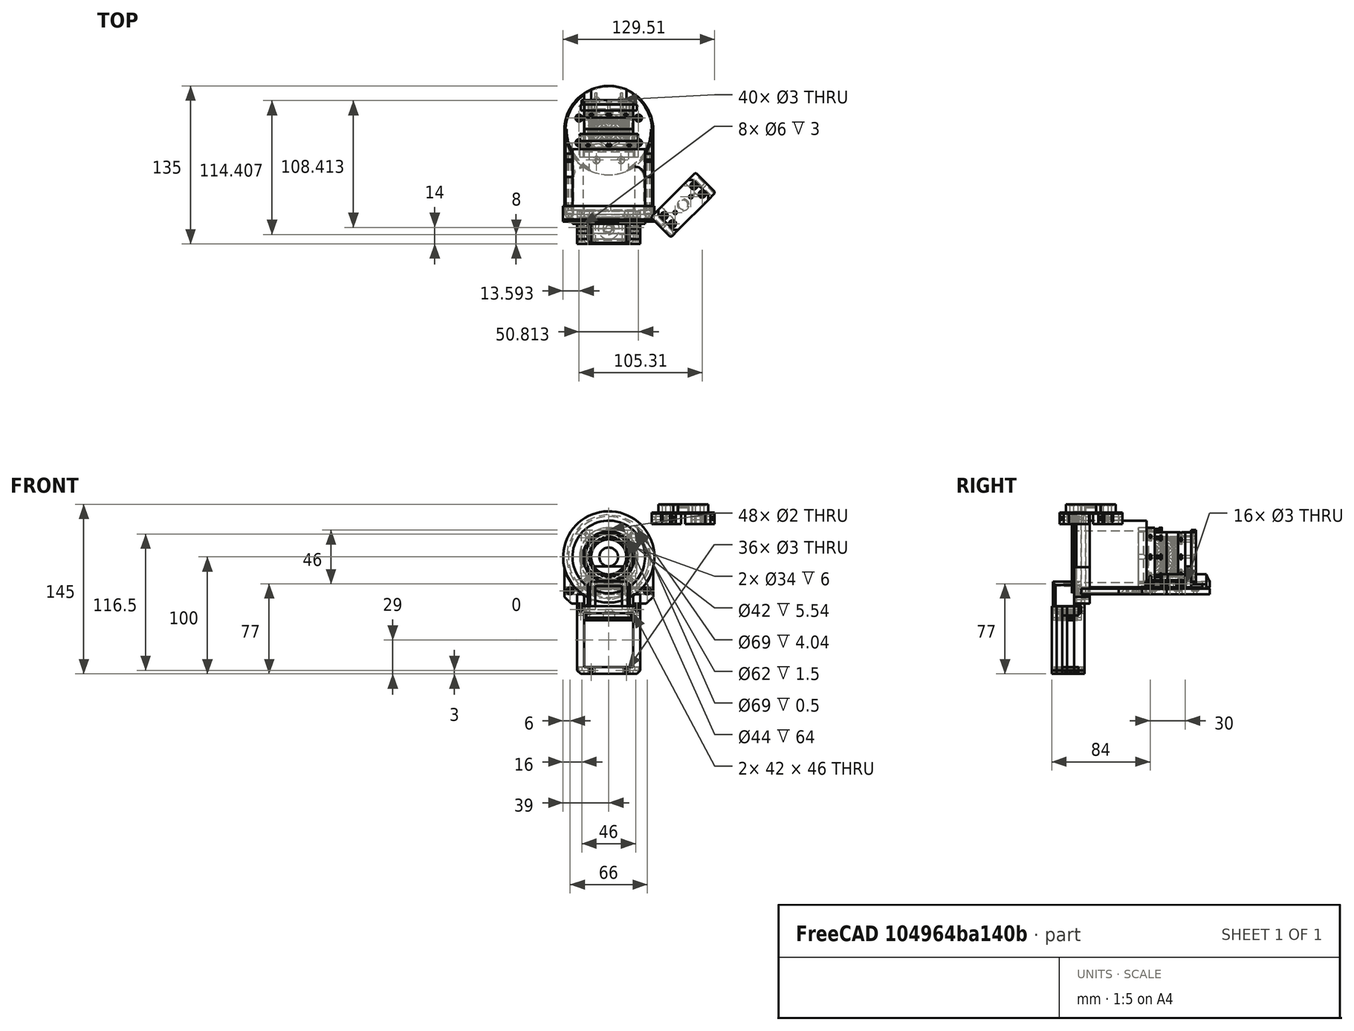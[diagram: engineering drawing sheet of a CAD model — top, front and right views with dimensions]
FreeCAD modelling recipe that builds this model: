
FCSTD DOCUMENT  (FreeCAD 0.19R24276 (Git))
Label: G-mini_encoder-holder_026
License: All rights reserved
LicenseURL: http://en.wikipedia.org/wiki/All_rights_reserved
objects: Part::Cylinder×239, Part::Cut×117, Part::Compound×116, Part::Box×114, Part::Chamfer×42, Part::FeaturePython×24, Mesh::Feature×17, Part::Common×9, Part::Torus×2
note: 663 computed .brp shape members not serialized (recipe doc carries the construction recipe); baked Part::Feature solids carry a one-line shape summary decoded from their .brp

FEATURE [Part::Box] Box883  label="Krychle882"
  AttacherType = Attacher::AttachEngine3D
  Height = 32
  Length = 15
  Placement = pos=(-38,-68,5) rot=(0,0,1;0rad)
  Width = 13.5
FEATURE [Part::Box] Box908  label="Krychle907"
  AttacherType = Attacher::AttachEngine3D
  Height = 6
  Length = 8
  Placement = pos=(-38,-79,5) rot=(0,0,1;0rad)
  Width = 80
FEATURE [Part::Box] Box909  label="Krychle908"
  AttacherType = Attacher::AttachEngine3D
  Height = 6
  Length = 8
  Placement = pos=(30,-79,5) rot=(0,0,1;0rad)
  Width = 80
FEATURE [Part::Box] Box910  label="Krychle909"
  AttacherType = Attacher::AttachEngine3D
  Height = 6
  Length = 20
  Placement = pos=(-38,-40,5) rot=(0,0,1;0rad)
  Width = 20
FEATURE [Part::Cylinder] Cylinder2670  label="Válec2640"
  Angle = 360
  AttacherType = Attacher::AttachEngine3D
  Height = 16
  Placement = pos=(-22,-40,0) rot=(0,0,1;0rad)
  Radius = 8
FEATURE [Part::Cylinder] Cylinder2671  label="Válec2641"
  Angle = 360
  AttacherType = Attacher::AttachEngine3D
  Height = 16
  Placement = pos=(22,-40,0) rot=(0,0,1;0rad)
  Radius = 8
FEATURE [Part::Box] Box911  label="Krychle910"
  AttacherType = Attacher::AttachEngine3D
  Height = 6
  Length = 20
  Placement = pos=(18,-40,5) rot=(0,0,1;0rad)
  Width = 20
FEATURE [Part::Cylinder] Cylinder2672  label="Válec2642"
  Angle = 360
  AttacherType = Attacher::AttachEngine3D
  Height = 16
  Radius = 36
FEATURE [Part::Cylinder] Cylinder2673  label="Válec2643"
  Angle = 360
  AttacherType = Attacher::AttachEngine3D
  Height = 16
  Radius = 36
FEATURE [Part::Cylinder] Cylinder2674  label="Válec2644"
  Angle = 360
  AttacherType = Attacher::AttachEngine3D
  Height = 16
  Radius = 36
FEATURE [Part::Chamfer] Chamfer132
  Base = -> Box908
  Edges = 1 edges r=1: [Edge2]
FEATURE [Part::Chamfer] Chamfer133
  Base = -> Box909
  Edges = 1 edges r=1: [Edge6]
FEATURE [Part::Compound] Compound1181
  Links = -> [Box911,Box910]
FEATURE [Part::Compound] Compound1182
  Links = -> [Cylinder2671,Cylinder2670]
FEATURE [Part::Chamfer] Chamfer135
  Base = -> Chamfer133
  Edges = 1 edges r=1: [Edge15]
FEATURE [Part::Chamfer] Chamfer139
  Base = -> Chamfer132
  Edges = 1 edges r=1: [Edge15]
FEATURE [Part::Cut] Cut996
  Base = -> Chamfer135
  Tool = -> Cylinder2674
FEATURE [Part::Cut] Cut994
  Base = -> Chamfer139
  Tool = -> Cylinder2672
FEATURE [Part::Cut] Cut993
  Base = -> Compound1181
  Tool = -> Compound1182
FEATURE [Part::Chamfer] Chamfer134
  Base = -> Cut993
  Edges = 1 edges r=1: [Edge8]
FEATURE [Part::Chamfer] Chamfer136
  Base = -> Chamfer134
  Edges = 1 edges r=1: [Edge8]
FEATURE [Part::Chamfer] Chamfer137
  Base = -> Chamfer136
  Edges = 1 edges r=1: [Edge23]
FEATURE [Part::Chamfer] Chamfer138
  Base = -> Chamfer137
  Edges = 1 edges r=1: [Edge16]
FEATURE [Part::Cut] Cut995
  Base = -> Chamfer138
  Tool = -> Cylinder2673
FEATURE [Part::Box] Box884  label="Krychle883"
  AttacherType = Attacher::AttachEngine3D
  Height = 32
  Length = 15
  Placement = pos=(23,-68,5) rot=(0,0,1;0rad)
  Width = 13.5
FEATURE [Part::Cylinder] Cylinder2630  label="Válec2600"
  Angle = 360
  AttacherType = Attacher::AttachEngine3D
  Height = 3
  Placement = pos=(-19.4454,-19.4454,19) rot=(0,0,1;2.35619rad)
  Radius = 3
FEATURE [Part::Cylinder] Cylinder2631  label="Válec2601"
  Angle = 360
  AttacherType = Attacher::AttachEngine3D
  Height = 5
  Placement = pos=(1.1e-14,-27.5,19.5) rot=(0,0,1;3.14159rad)
  Radius = 3
FEATURE [Part::Cylinder] Cylinder2632  label="Válec2602"
  Angle = 360
  AttacherType = Attacher::AttachEngine3D
  Height = 20
  Placement = pos=(-19.4454,19.4454,19) rot=(0,0,1;0.785398rad)
  Radius = 1.5
FEATURE [Part::Cylinder] Cylinder2633  label="Válec2603"
  Angle = 360
  AttacherType = Attacher::AttachEngine3D
  Height = 20
  Placement = pos=(-19.4454,-19.4454,19) rot=(0,0,1;2.35619rad)
  Radius = 1.5
FEATURE [Part::Cylinder] Cylinder2634  label="Válec2604"
  Angle = 360
  AttacherType = Attacher::AttachEngine3D
  Height = 20
  Placement = pos=(19.4454,-19.4454,19) rot=(0,0,1;3.92699rad)
  Radius = 1.5
FEATURE [Part::Cylinder] Cylinder2635  label="Válec2605"
  Angle = 360
  AttacherType = Attacher::AttachEngine3D
  Height = 3
  Placement = pos=(-19.45,19.45,19) rot=(0,0,1;0.785398rad)
  Radius = 3
FEATURE [Part::Cylinder] Cylinder2636  label="Válec2606"
  Angle = 360
  AttacherType = Attacher::AttachEngine3D
  Height = 3
  Placement = pos=(-27.5,-4e-15,19) rot=(0,0,1;1.5708rad)
  Radius = 3
FEATURE [Part::Cylinder] Cylinder2637  label="Válec2607"
  Angle = 360
  AttacherType = Attacher::AttachEngine3D
  Height = 5
  Placement = pos=(19.45,-19.45,19.5) rot=(0,0,1;3.92699rad)
  Radius = 3
FEATURE [Part::Cylinder] Cylinder2638  label="Válec2608"
  Angle = 360
  AttacherType = Attacher::AttachEngine3D
  Height = 3
  Placement = pos=(27.5,1.2e-14,19) rot=(0,0,-1;1.5708rad)
  Radius = 3
FEATURE [Part::Cylinder] Cylinder2639  label="Válec2609"
  Angle = 360
  AttacherType = Attacher::AttachEngine3D
  Height = 3
  Placement = pos=(19.4454,19.4454,19) rot=(0,0,-1;0.785398rad)
  Radius = 3
FEATURE [Part::FeaturePython] Tube120  # WARN: FeaturePython — macro-defined, semantics opaque (R4)
  AttacherType = Attacher::AttachEngine3D
  Height = 24
  InnerRadius = 22
  OuterRadius = 31
  Placement = pos=(0,-17,37) rot=(1,0,0;1.5708rad)
FEATURE [Part::Cylinder] Cylinder2640  label="Válec2610"
  Angle = 360
  AttacherType = Attacher::AttachEngine3D
  Height = 20
  Placement = pos=(-27.5,-4e-15,19) rot=(0,0,1;1.5708rad)
  Radius = 1.5
FEATURE [Part::Cylinder] Cylinder2641  label="Válec2611"
  Angle = 360
  AttacherType = Attacher::AttachEngine3D
  Height = 20
  Placement = pos=(1.1e-14,-27.5,19) rot=(0,0,1;3.14159rad)
  Radius = 1.5
FEATURE [Part::Cylinder] Cylinder2642  label="Válec2612"
  Angle = 360
  AttacherType = Attacher::AttachEngine3D
  Height = 3
  Placement = pos=(0,27.5,19) rot=(0,0,1;0rad)
  Radius = 3
FEATURE [Part::Compound] Compound1170
  Links = -> [Cylinder2642,Cylinder2635,Cylinder2636,Cylinder2630,Cylinder2631,Cylinder2637,Cylinder2638,Cylinder2639]
  Placement = pos=(0,0,-19) rot=(0,0,1;0rad)
FEATURE [Part::Cylinder] Cylinder2643  label="Válec2613"
  Angle = 360
  AttacherType = Attacher::AttachEngine3D
  Height = 20
  Placement = pos=(19.4454,19.4454,19) rot=(0,0,-1;0.785398rad)
  Radius = 1.5
FEATURE [Part::Cylinder] Cylinder2644  label="Válec2614"
  Angle = 360
  AttacherType = Attacher::AttachEngine3D
  Height = 20
  Placement = pos=(27.5,1.2e-14,19) rot=(0,0,-1;1.5708rad)
  Radius = 1.5
FEATURE [Part::Cylinder] Cylinder2645  label="Válec2615"
  Angle = 360
  AttacherType = Attacher::AttachEngine3D
  Height = 6
  Radius = 38
FEATURE [Part::Cut] Cut630
  Base = -> Cylinder2645
  Tool = -> Compound1170
FEATURE [Part::Cylinder] Cylinder2646  label="Válec2616"
  Angle = 360
  AttacherType = Attacher::AttachEngine3D
  Height = 20
  Placement = pos=(0,27.5,19) rot=(0,0,1;0rad)
  Radius = 1.5
FEATURE [Part::Compound] Compound1169
  Links = -> [Cylinder2646,Cylinder2632,Cylinder2640,Cylinder2633,Cylinder2641,Cylinder2634,Cylinder2644,Cylinder2643]
  Placement = pos=(0,0,-23) rot=(0,0,1;0rad)
FEATURE [Part::Cut] Cut628
  Base = -> Cut630
  Tool = -> Compound1169
FEATURE [Part::Cylinder] Cylinder2647  label="Válec2617"
  Angle = 360
  AttacherType = Attacher::AttachEngine3D
  Height = 5
  Placement = pos=(0,0,1) rot=(0,0,1;0rad)
  Radius = 14
FEATURE [Part::Cut] Cut629
  Base = -> Cut628
  Tool = -> Cylinder2647
FEATURE [Part::Chamfer] Chamfer126
  Base = -> Cut629
  Edges = 1 edges r=1: [Edge3]
  Placement = pos=(1e-15,0,11) rot=(-0.19509,0.980785,0;3.14159rad)
FEATURE [Part::Cut] Cut976
  Base = -> Chamfer126
  Tool = -> Tube120
FEATURE [Part::Compound] Compound
  Links = -> [Box884,Box883]
  Placement = pos=(0,-17.5,0) rot=(0,0,1;0rad)
FEATURE [Part::Box] Box912  label="Krychle911"
  AttacherType = Attacher::AttachEngine3D
  Height = 40
  Length = 17
  Placement = pos=(21,-68,-3) rot=(0,0,1;0rad)
  Width = 13.5
FEATURE [Part::Box] Box913  label="Krychle912"
  AttacherType = Attacher::AttachEngine3D
  Height = 40
  Length = 17
  Placement = pos=(-38,-68,-3) rot=(0,0,1;0rad)
  Width = 13.5
FEATURE [Part::Compound] Compound1184
  Links = -> [Box912,Box913]
  Placement = pos=(0,-6,0) rot=(0,0,1;0rad)
FEATURE [Part::Compound] Compound1185
  Links = -> [Cut996,Cut994]
FEATURE [Part::Cylinder] Cylinder2621  label="Válec2591"
  Angle = 360
  AttacherType = Attacher::AttachEngine3D
  Height = 50
  Placement = pos=(-34,-10,8) rot=(1,0,0;1.5708rad)
  Radius = 1.5
FEATURE [Part::Cylinder] Cylinder2622  label="Válec2592"
  Angle = 360
  AttacherType = Attacher::AttachEngine3D
  Height = 8
  Placement = pos=(-34,-61,8) rot=(1,0,0;1.5708rad)
  Radius = 3
FEATURE [Part::Cylinder] Cylinder2623  label="Válec2593"
  Angle = 360
  AttacherType = Attacher::AttachEngine3D
  Height = 50
  Placement = pos=(34,-10,8) rot=(1,0,0;1.5708rad)
  Radius = 1.5
FEATURE [Part::Cylinder] Cylinder2624  label="Válec2594"
  Angle = 360
  AttacherType = Attacher::AttachEngine3D
  Height = 8
  Placement = pos=(34,-61,8) rot=(1,0,0;1.5708rad)
  Radius = 3
FEATURE [Part::Compound] Compound1186
  Links = -> [Cylinder2621,Cylinder2623]
  Placement = pos=(0,-11,0) rot=(0,0,1;0rad)
FEATURE [Part::Compound] Compound1187
  Links = -> [Cylinder2622,Cylinder2624]
  Placement = pos=(0,-5,0) rot=(0,0,1;0rad)
FEATURE [Part::Cylinder] Cylinder2675  label="Válec2645"
  Angle = 360
  AttacherType = Attacher::AttachEngine3D
  Height = 16
  Radius = 38
FEATURE [Part::Cylinder] Cylinder2676  label="Válec2646"
  Angle = 360
  AttacherType = Attacher::AttachEngine3D
  Height = 16
  Radius = 38
FEATURE [Part::Box] Box914  label="Krychle913"
  AttacherType = Attacher::AttachEngine3D
  Height = 6
  Length = 8
  Placement = pos=(-38,-68,5) rot=(0,0,1;0rad)
  Width = 69
FEATURE [Part::Box] Box915  label="Krychle914"
  AttacherType = Attacher::AttachEngine3D
  Height = 6
  Length = 8
  Placement = pos=(30,-68,5) rot=(0,0,1;0rad)
  Width = 69
FEATURE [Part::Chamfer] Chamfer142
  Base = -> Box915
  Edges = 1 edges r=1: [Edge6]
FEATURE [Part::Chamfer] Chamfer140
  Base = -> Chamfer142
  Edges = 1 edges r=1: [Edge15]
FEATURE [Part::Chamfer] Chamfer143
  Base = -> Box914
  Edges = 1 edges r=1: [Edge2]
FEATURE [Part::Chamfer] Chamfer141
  Base = -> Chamfer143
  Edges = 1 edges r=1: [Edge15]
FEATURE [Part::Cut] Cut997
  Base = -> Chamfer141
  Tool = -> Cylinder2675
FEATURE [Part::Cut] Cut998
  Base = -> Chamfer140
  Tool = -> Cylinder2676
FEATURE [Part::Compound] Compound1188
  Links = -> [Cut998,Cut997]
FEATURE [Part::Cut] Cut
  Base = -> Compound1184
  Tool = -> Compound1188
FEATURE [Part::Cylinder] Cylinder2650  label="Válec2620"
  Angle = 360
  AttacherType = Attacher::AttachEngine3D
  Height = 60
  Placement = pos=(24,73,-80) rot=(0,0,1;0rad)
  Radius = 1.5
FEATURE [Part::Cylinder] Cylinder2651  label="Válec2621"
  Angle = 360
  AttacherType = Attacher::AttachEngine3D
  Height = 60
  Placement = pos=(-24,73,-80) rot=(0,0,1;0rad)
  Radius = 1.5
FEATURE [Part::Cylinder] Cylinder2652  label="Válec2622"
  Angle = 360
  AttacherType = Attacher::AttachEngine3D
  Height = 60
  Placement = pos=(-15,125,-80) rot=(0,0,1;0rad)
  Radius = 1.5
FEATURE [Part::Cylinder] Cylinder2653  label="Válec2623"
  Angle = 360
  AttacherType = Attacher::AttachEngine3D
  Height = 60
  Placement = pos=(15,125,-80) rot=(0,0,1;0rad)
  Radius = 1.5
FEATURE [Part::Box] Box893  label="Krychle892"
  AttacherType = Attacher::AttachEngine3D
  Height = 9
  Length = 54
  Placement = pos=(-27,60,76) rot=(0,0,1;0rad)
  Width = 68
FEATURE [Part::Box] Box894  label="Krychle893"
  AttacherType = Attacher::AttachEngine3D
  Height = 50
  Length = 42
  Placement = pos=(-21,58,40) rot=(0,0,1;0rad)
  Width = 64
FEATURE [Part::Cut] Cut978
  Base = -> Box893
  Placement = pos=(0,0,-9) rot=(0,0,1;0rad)
  Tool = -> Box894
FEATURE [Part::Compound] Compound1172
  Links = -> [Cylinder2650,Cylinder2651,Cylinder2652,Cylinder2653]
  Placement = pos=(0,0,120) rot=(0,0,1;0rad)
FEATURE [Part::Chamfer] Chamfer127
  Base = -> Cut978
  Edges = 2 edges r=3: [Edge3,Edge15]
FEATURE [Part::Cut] Cut979
  Base = -> Chamfer127
  Tool = -> Compound1172
FEATURE [Part::Box] Box904  label="Krychle903"
  AttacherType = Attacher::AttachEngine3D
  Height = 2
  Length = 7
  Placement = pos=(-28,70,-48) rot=(0,0,1;0rad)
  Width = 6
FEATURE [Part::Box] Box905  label="Krychle904"
  AttacherType = Attacher::AttachEngine3D
  Height = 2
  Length = 6
  Placement = pos=(-18,122,-48) rot=(0,0,1;0rad)
  Width = 6
FEATURE [Part::Box] Box906  label="Krychle905"
  AttacherType = Attacher::AttachEngine3D
  Height = 2
  Length = 6
  Placement = pos=(21,70,-48) rot=(0,0,1;0rad)
  Width = 6
FEATURE [Part::Box] Box907  label="Krychle906"
  AttacherType = Attacher::AttachEngine3D
  Height = 2
  Length = 6
  Placement = pos=(12,122,-48) rot=(0,0,1;0rad)
  Width = 6
FEATURE [Part::Compound] Compound1179
  Links = -> [Box904,Box905,Box906,Box907]
  Placement = pos=(0,0,118) rot=(0,0,1;0rad)
FEATURE [Part::Cut] Cut989
  Base = -> Cut979
  Placement = pos=(0,2,65) rot=(0,0.707107,-0.707107;3.14159rad)
  Tool = -> Compound1179
FEATURE [Part::Torus] Torus004  label="Anuloid004"
  Angle1 = -180
  Angle2 = 180
  Angle3 = 360
  AttacherType = Attacher::AttachEngine3D
  Placement = pos=(17,-98,10) rot=(1,0,0;1.5708rad)
  Radius1 = 34.1
  Radius2 = 2
FEATURE [Part::FeaturePython] Tube115  # WARN: FeaturePython — macro-defined, semantics opaque (R4)
  AttacherType = Attacher::AttachEngine3D
  Height = 11.5
  InnerRadius = 34.5
  OuterRadius = 39
  Placement = pos=(17,-92,10) rot=(1,0,0;1.5708rad)
FEATURE [Part::FeaturePython] Tube116  # WARN: FeaturePython — macro-defined, semantics opaque (R4)
  AttacherType = Attacher::AttachEngine3D
  Height = 0.5
  InnerRadius = 34.5
  OuterRadius = 39
  Placement = pos=(17,-93.5,10) rot=(1,0,0;1.5708rad)
FEATURE [Part::FeaturePython] Tube117  # WARN: FeaturePython — macro-defined, semantics opaque (R4)
  AttacherType = Attacher::AttachEngine3D
  Height = 1.5
  InnerRadius = 31
  OuterRadius = 39
  Placement = pos=(17,-92,10) rot=(1,0,0;1.5708rad)
FEATURE [Part::Cut] Cut969
  Base = -> Tube115
  Tool = -> Torus004
FEATURE [Part::Compound] Compound1161
  Links = -> [Tube117,Tube116]
FEATURE [Part::Cylinder] Cylinder2620  label="Válec2590"
  Angle = 360
  AttacherType = Attacher::AttachEngine3D
  Height = 10
  Placement = pos=(17,-98,44) rot=(1,0,0;1.5708rad)
  Radius = 2
FEATURE [Part::Cut] Cut970
  Base = -> Cut969
  Placement = pos=(0,-2,0) rot=(0,0,1;0rad)
  Tool = -> Cylinder2620
FEATURE [Part::Compound] Compound1162  label="Wrist_outer-halo-ring"
  Links = -> [Cut970,Compound1161]
  Placement = pos=(-17,-166,47) rot=(1,0,0;3.14159rad)
FEATURE [Part::Cylinder] Cylinder  label="Válec"
  Angle = 360
  AttacherType = Attacher::AttachEngine3D
  Height = 20
  Placement = pos=(0,-54,37) rot=(1,0,0;1.5708rad)
  Radius = 39
FEATURE [Part::Cut] Cut999
  Base = -> Cut
  Tool = -> Cylinder
FEATURE [Part::Chamfer] Chamfer
  Base = -> Cut999
  Edges = 2 edges r=6: [Edge18,Edge36]
FEATURE [Part::FeaturePython] Tube121  # WARN: FeaturePython — macro-defined, semantics opaque (R4)
  AttacherType = Attacher::AttachEngine3D
  Height = 64
  InnerRadius = 22
  OuterRadius = 31
  Placement = pos=(0,-16,37) rot=(1,0,0;1.5708rad)
FEATURE [Part::Cylinder] Cylinder2677  label="Válec2647"
  Angle = 360
  AttacherType = Attacher::AttachEngine3D
  Height = 3
  Placement = pos=(-33,-61,8) rot=(1,0,0;1.5708rad)
  Radius = 3
FEATURE [Part::Cylinder] Cylinder2678  label="Válec2648"
  Angle = 360
  AttacherType = Attacher::AttachEngine3D
  Height = 3
  Placement = pos=(33,-61,8) rot=(1,0,0;1.5708rad)
  Radius = 3
FEATURE [Part::Compound] Compound1189
  Links = -> [Cylinder2677,Cylinder2678]
  Placement = pos=(0,-10,0) rot=(0,0,1;0rad)
FEATURE [Part::Cylinder] Cylinder2679  label="Válec2649"
  Angle = 360
  AttacherType = Attacher::AttachEngine3D
  Height = 60
  Placement = pos=(-33,-10,8) rot=(1,0,0;1.5708rad)
  Radius = 1.5
FEATURE [Part::Cylinder] Cylinder2680  label="Válec2650"
  Angle = 360
  AttacherType = Attacher::AttachEngine3D
  Height = 60
  Placement = pos=(33,-10,8) rot=(1,0,0;1.5708rad)
  Radius = 1.5
FEATURE [Part::Compound] Compound1190
  Links = -> [Cylinder2679,Cylinder2680]
  Placement = pos=(0,-4,0) rot=(0,0,1;0rad)
FEATURE [Part::Cut] Cut1000
  Base = -> Chamfer
  Tool = -> Compound1189
FEATURE [Part::Cut] Cut1001
  Base = -> Cut1000
  Tool = -> Compound1190
FEATURE [Part::Cut] Cut1002
  Base = -> Compound1185
  Tool = -> Compound
FEATURE [Part::Box] Box  label="Krychle"
  AttacherType = Attacher::AttachEngine3D
  Height = 6
  Length = 6
  Placement = pos=(30,-27,5) rot=(0,0,1;0rad)
  Width = 2
FEATURE [Part::Box] Box916  label="Krychle915"
  AttacherType = Attacher::AttachEngine3D
  Height = 6
  Length = 6
  Placement = pos=(-36,-27,5) rot=(0,0,1;0rad)
  Width = 2
FEATURE [Part::Compound] Compound1191
  Links = -> [Box,Box916]
FEATURE [Part::Cut] Cut1003
  Base = -> Cut1002
  Tool = -> Compound1191
FEATURE [Part::Box] Box917  label="Krychle916"
  AttacherType = Attacher::AttachEngine3D
  Height = 6
  Length = 6
  Placement = pos=(30,-27,5) rot=(0,0,1;0rad)
  Width = 2
FEATURE [Part::Box] Box918  label="Krychle917"
  AttacherType = Attacher::AttachEngine3D
  Height = 6
  Length = 6
  Placement = pos=(-36,-27,5) rot=(0,0,1;0rad)
  Width = 2
FEATURE [Part::Compound] Compound1192
  Links = -> [Box917,Box918]
FEATURE [Part::Cut] Cut1004
  Base = -> Cut995
  Tool = -> Compound1192
FEATURE [Part::Cylinder] Cylinder2681  label="Válec2651"
  Angle = 360
  AttacherType = Attacher::AttachEngine3D
  Height = 60
  Placement = pos=(-33,-10,8) rot=(1,0,0;1.5708rad)
  Radius = 1.5
FEATURE [Part::Cylinder] Cylinder2682  label="Válec2652"
  Angle = 360
  AttacherType = Attacher::AttachEngine3D
  Height = 60
  Placement = pos=(33,-10,8) rot=(1,0,0;1.5708rad)
  Radius = 1.5
FEATURE [Part::Compound] Compound1193
  Links = -> [Cylinder2681,Cylinder2682]
  Placement = pos=(0,-1,0) rot=(0,0,1;0rad)
FEATURE [Part::Cylinder] Cylinder2683  label="Válec2653"
  Angle = 360
  AttacherType = Attacher::AttachEngine3D
  Height = 100
  Placement = pos=(-33,-10,8) rot=(1,0,0;1.5708rad)
  Radius = 1.5
FEATURE [Part::Cylinder] Cylinder2684  label="Válec2654"
  Angle = 360
  AttacherType = Attacher::AttachEngine3D
  Height = 100
  Placement = pos=(33,-10,8) rot=(1,0,0;1.5708rad)
  Radius = 1.5
FEATURE [Part::Compound] Compound1194
  Links = -> [Cylinder2683,Cylinder2684]
  Placement = pos=(0,-1,0) rot=(0,0,1;0rad)
FEATURE [Part::Cut] Cut1005
  Base = -> Cut1003
  Tool = -> Compound1194
FEATURE [Part::Cut] Cut1006
  Base = -> Cut976
  Tool = -> Compound1193
FEATURE [Part::Cylinder] Cylinder2685  label="Válec2655"
  Angle = 360
  AttacherType = Attacher::AttachEngine3D
  Height = 60
  Placement = pos=(-33,-10,8) rot=(1,0,0;1.5708rad)
  Radius = 1.5
FEATURE [Part::Cylinder] Cylinder2686  label="Válec2656"
  Angle = 360
  AttacherType = Attacher::AttachEngine3D
  Height = 60
  Placement = pos=(33,-10,8) rot=(1,0,0;1.5708rad)
  Radius = 1.5
FEATURE [Part::Compound] Compound1195
  Links = -> [Cylinder2685,Cylinder2686]
  Placement = pos=(0,-4,0) rot=(0,0,1;0rad)
FEATURE [Part::Cut] Cut1007
  Base = -> Cut1004
  Tool = -> Compound1195
FEATURE [Part::Box] Box895  label="Krychle894"
  AttacherType = Attacher::AttachEngine3D
  Height = 9
  Length = 54
  Placement = pos=(-27,70,75) rot=(0,0,1;0rad)
  Width = 58
FEATURE [Part::Box] Box896  label="Krychle895"
  AttacherType = Attacher::AttachEngine3D
  Height = 50
  Length = 42
  Placement = pos=(-21,76,38) rot=(0,0,1;0rad)
  Width = 46
FEATURE [Part::Cylinder] Cylinder2658  label="Válec2628"
  Angle = 360
  AttacherType = Attacher::AttachEngine3D
  Height = 60
  Placement = pos=(24,73,-80) rot=(0,0,1;0rad)
  Radius = 1.5
FEATURE [Part::Cylinder] Cylinder2659  label="Válec2629"
  Angle = 360
  AttacherType = Attacher::AttachEngine3D
  Height = 60
  Placement = pos=(-24,73,-80) rot=(0,0,1;0rad)
  Radius = 1.5
FEATURE [Part::Cylinder] Cylinder2660  label="Válec2630"
  Angle = 360
  AttacherType = Attacher::AttachEngine3D
  Height = 60
  Placement = pos=(-15,125,-80) rot=(0,0,1;0rad)
  Radius = 1.5
FEATURE [Part::Cylinder] Cylinder2661  label="Válec2631"
  Angle = 360
  AttacherType = Attacher::AttachEngine3D
  Height = 60
  Placement = pos=(15,125,-80) rot=(0,0,1;0rad)
  Radius = 1.5
FEATURE [Part::Box] Box897  label="Krychle896"
  AttacherType = Attacher::AttachEngine3D
  Height = 10
  Length = 54
  Placement = pos=(-27,70,75) rot=(0,0,1;0rad)
  Width = 58
FEATURE [Part::Box] Box898  label="Krychle897"
  AttacherType = Attacher::AttachEngine3D
  Height = 50
  Length = 42
  Placement = pos=(-21,76,38) rot=(0,0,1;0rad)
  Width = 46
FEATURE [Part::Cylinder] Cylinder2662  label="Válec2632"
  Angle = 360
  AttacherType = Attacher::AttachEngine3D
  Height = 3
  Placement = pos=(-24,128,72) rot=(1,0,0;1.5708rad)
  Radius = 3
FEATURE [Part::Cylinder] Cylinder2663  label="Válec2633"
  Angle = 360
  AttacherType = Attacher::AttachEngine3D
  Height = 3
  Placement = pos=(24,128,72) rot=(1,0,0;1.5708rad)
  Radius = 3
FEATURE [Part::Compound] Compound1174
  Links = -> [Cylinder2658,Cylinder2659,Cylinder2660,Cylinder2661]
  Placement = pos=(0,0,120) rot=(0,0,1;0rad)
FEATURE [Part::Cut] Cut981
  Base = -> Box895
  Placement = pos=(0,0,10) rot=(0,0,1;0rad)
  Tool = -> Box896
FEATURE [Part::Cut] Cut983
  Base = -> Box897
  Tool = -> Box898
FEATURE [Part::Compound] Compound1175
  Links = -> [Cylinder2662,Cylinder2663]
  Placement = pos=(0,0,8) rot=(0,0,1;0rad)
FEATURE [Part::Cylinder] Cylinder2664  label="Válec2634"
  Angle = 360
  AttacherType = Attacher::AttachEngine3D
  Height = 50
  Placement = pos=(-24,140,72) rot=(1,0,0;1.5708rad)
  Radius = 1.5
FEATURE [Part::Cylinder] Cylinder2665  label="Válec2635"
  Angle = 360
  AttacherType = Attacher::AttachEngine3D
  Height = 50
  Placement = pos=(24,140,72) rot=(1,0,0;1.5708rad)
  Radius = 1.5
FEATURE [Part::Compound] Compound1177
  Links = -> [Cylinder2664,Cylinder2665]
  Placement = pos=(0,0,8) rot=(0,0,1;0rad)
FEATURE [Part::Box] Box903  label="Krychle902"
  AttacherType = Attacher::AttachEngine3D
  Height = 10
  Length = 56
  Placement = pos=(-28,78,75) rot=(0,0,1;0rad)
  Width = 44
FEATURE [Part::Cut] Cut984
  Base = -> Cut983
  Tool = -> Box903
FEATURE [Part::Cylinder] Cylinder2666  label="Válec2636"
  Angle = 360
  AttacherType = Attacher::AttachEngine3D
  Height = 60
  Placement = pos=(15,125,-80) rot=(0,0,1;0rad)
  Radius = 1.5
FEATURE [Part::Cylinder] Cylinder2667  label="Válec2637"
  Angle = 360
  AttacherType = Attacher::AttachEngine3D
  Height = 60
  Placement = pos=(24,73,-80) rot=(0,0,1;0rad)
  Radius = 1.5
FEATURE [Part::Cylinder] Cylinder2668  label="Válec2638"
  Angle = 360
  AttacherType = Attacher::AttachEngine3D
  Height = 60
  Placement = pos=(-24,73,-80) rot=(0,0,1;0rad)
  Radius = 1.5
FEATURE [Part::Cylinder] Cylinder2669  label="Válec2639"
  Angle = 360
  AttacherType = Attacher::AttachEngine3D
  Height = 60
  Placement = pos=(-15,125,-80) rot=(0,0,1;0rad)
  Radius = 1.5
FEATURE [Part::Compound] Compound1178
  Links = -> [Cylinder2667,Cylinder2668,Cylinder2669,Cylinder2666]
  Placement = pos=(0,0,120) rot=(0,0,1;0rad)
FEATURE [Part::Cut] Cut985
  Base = -> Cut984
  Tool = -> Compound1178
FEATURE [Part::Chamfer] Chamfer130
  Base = -> Cut981
  Edges = 2 edges r=3: [Edge3,Edge15]
FEATURE [Part::Cut] Cut990
  Base = -> Chamfer130
  Tool = -> Compound1174
FEATURE [Part::Chamfer] Chamfer131
  Base = -> Cut985
  Edges = 2 edges r=3: [Edge32,Edge43]
FEATURE [Part::Cut] Cut991
  Base = -> Chamfer131
  Tool = -> Compound1175
FEATURE [Part::Cut] Cut992
  Base = -> Cut991
  Tool = -> Compound1177
FEATURE [Part::Compound] Compound1180  label="G-mini_encoder-holder-front"
  Links = -> [Cut990,Cut992]
  Placement = pos=(0,1,65) rot=(0,0.707107,-0.707107;3.14159rad)
FEATURE [Part::Box] Box919  label="Krychle918"
  AttacherType = Attacher::AttachEngine3D
  Height = 16
  Length = 12
  Placement = pos=(9,-74,-11) rot=(0,0,1;0rad)
  Width = 9
FEATURE [Part::Box] Box920  label="Krychle919"
  AttacherType = Attacher::AttachEngine3D
  Height = 16
  Length = 12
  Placement = pos=(-21,-74,-11) rot=(0,0,1;0rad)
  Width = 9
FEATURE [Part::Compound] Compound1196
  Links = -> [Box919,Box920]
FEATURE [Part::Cylinder] Cylinder2687  label="Válec2657"
  Angle = 360
  AttacherType = Attacher::AttachEngine3D
  Height = 14
  Placement = pos=(9,-60,-11) rot=(1,0,0;1.5708rad)
  Radius = 12
FEATURE [Part::Cylinder] Cylinder2688  label="Válec2658"
  Angle = 360
  AttacherType = Attacher::AttachEngine3D
  Height = 14
  Placement = pos=(-9,-60,-11) rot=(1,0,0;1.5708rad)
  Radius = 12
FEATURE [Part::Compound] Compound1197
  Links = -> [Cylinder2687,Cylinder2688]
FEATURE [Part::Cut] Cut1008
  Base = -> Compound1196
  Tool = -> Compound1197
FEATURE [Part::Cylinder] Cylinder2689  label="Válec2659"
  Angle = 360
  AttacherType = Attacher::AttachEngine3D
  Height = 20
  Placement = pos=(0,-54,37) rot=(1,0,0;1.5708rad)
  Radius = 39
FEATURE [Part::Cut] Cut1009
  Base = -> Cut1008
  Tool = -> Cylinder2689
FEATURE [Part::Compound] Compound1199  label="Wrist_outer-halo-encoder"
  Links = -> [Cut1009,Cut1001,Compound1162,Cut989]
  Placement = pos=(0,-4,0) rot=(0,0,1;0rad)
FEATURE [Mesh::Feature] Mesh  label="Wrist_outer-halo-encoder (Meshed)"
FEATURE [Part::FeaturePython] Tube125  # WARN: FeaturePython — macro-defined, semantics opaque (R4)
  AttacherType = Attacher::AttachEngine3D
  Height = 1
  InnerRadius = 12
  OuterRadius = 14
  Placement = pos=(0,0,9) rot=(0,0,1;0rad)
FEATURE [Part::Cylinder] Cylinder2648  label="Válec2618"
  Angle = 360
  AttacherType = Attacher::AttachEngine3D
  Height = 20
  Radius = 38
FEATURE [Part::Box] Box887  label="Krychle886"
  AttacherType = Attacher::AttachEngine3D
  Height = 7
  Length = 6
  Placement = pos=(15,-17,10) rot=(0,0,1;0rad)
  Width = 54
FEATURE [Part::Box] Box888  label="Krychle887"
  AttacherType = Attacher::AttachEngine3D
  Height = 7
  Length = 6
  Placement = pos=(-21,-17,10) rot=(0,0,1;0rad)
  Width = 54
FEATURE [Part::Compound] Compound1171
  Links = -> [Box887,Box888]
FEATURE [Part::Common] Common006
  Base = -> Compound1171
  Tool = -> Cylinder2648
FEATURE [Part::Chamfer] Chamfer144
  Base = -> Common006
  Edges = 2 edges r=1: [Edge6,Edge13]
FEATURE [Part::Cylinder] Cylinder2690  label="Válec2660"
  Angle = 360
  AttacherType = Attacher::AttachEngine3D
  Height = 64
  Placement = pos=(-26,-11,13) rot=(0,1,0;1.5708rad)
  Radius = 1.5
FEATURE [Part::Cylinder] Cylinder2691  label="Válec2661"
  Angle = 360
  AttacherType = Attacher::AttachEngine3D
  Height = 3
  Placement = pos=(-26,-11,13) rot=(0,1,0;1.5708rad)
  Radius = 3
FEATURE [Part::Cylinder] Cylinder2693  label="Válec2663"
  Angle = 360
  AttacherType = Attacher::AttachEngine3D
  Height = 3
  Placement = pos=(-26,-11,13) rot=(0,1,0;1.5708rad)
  Radius = 3
FEATURE [Part::Cylinder] Cylinder2694  label="Válec2664"
  Angle = 360
  AttacherType = Attacher::AttachEngine3D
  Height = 3
  Placement = pos=(-26,1,13) rot=(0,1,0;1.5708rad)
  Radius = 3
FEATURE [Part::Cylinder] Cylinder2695  label="Válec2665"
  Angle = 360
  AttacherType = Attacher::AttachEngine3D
  Height = 64
  Placement = pos=(-26,1,13) rot=(0,1,0;1.5708rad)
  Radius = 1.5
FEATURE [Part::Cylinder] Cylinder2696  label="Válec2666"
  Angle = 360
  AttacherType = Attacher::AttachEngine3D
  Height = 64
  Placement = pos=(-26,14,13) rot=(0,1,0;1.5708rad)
  Radius = 1.5
FEATURE [Part::Compound] Compound1202
  Links = -> [Cylinder2695,Cylinder2690,Cylinder2696]
  Placement = pos=(0,-2,1) rot=(0,0,1;0rad)
FEATURE [Part::Cylinder] Cylinder2692  label="Válec2662"
  Angle = 360
  AttacherType = Attacher::AttachEngine3D
  Height = 3
  Placement = pos=(-26,14,13) rot=(0,1,0;1.5708rad)
  Radius = 3
FEATURE [Part::Compound] Compound1201
  Links = -> [Cylinder2694,Cylinder2691,Cylinder2692]
  Placement = pos=(5,-2,1) rot=(0,0,1;0rad)
FEATURE [Part::Cylinder] Cylinder2697  label="Válec2667"
  Angle = 360
  AttacherType = Attacher::AttachEngine3D
  Height = 3
  Placement = pos=(-26,14,13) rot=(0,1,0;1.5708rad)
  Radius = 3
FEATURE [Part::Cylinder] Cylinder2698  label="Válec2668"
  Angle = 360
  AttacherType = Attacher::AttachEngine3D
  Height = 3
  Placement = pos=(-26,1,13) rot=(0,1,0;1.5708rad)
  Radius = 3
FEATURE [Part::Compound] Compound1183
  Links = -> [Cylinder2698,Cylinder2693,Cylinder2697]
  Placement = pos=(44,-2,1) rot=(0,0,1;0rad)
FEATURE [Part::Cut] Cut988
  Base = -> Chamfer144
  Tool = -> Compound1183
FEATURE [Part::Cut] Cut1011
  Base = -> Cut988
  Tool = -> Compound1201
FEATURE [Part::Cut] Cut1010
  Base = -> Cut1011
  Tool = -> Compound1202
FEATURE [Part::Cylinder] Cylinder2755  label="Válec2725"
  Angle = 360
  AttacherType = Attacher::AttachEngine3D
  Height = 10
  Placement = pos=(20,0,17.5) rot=(0,0,1;0rad)
  Radius = 2.2
FEATURE [Part::Cylinder] Cylinder2756  label="Válec2726"
  Angle = 360
  AttacherType = Attacher::AttachEngine3D
  Height = 20
  Placement = pos=(0,23,8) rot=(0,0,1;0rad)
  Radius = 1
FEATURE [Part::Cylinder] Cylinder2757  label="Válec2727"
  Angle = 360
  AttacherType = Attacher::AttachEngine3D
  Height = 20
  Placement = pos=(-16.26,16.26,8) rot=(0,0,1;0.785398rad)
  Radius = 1
FEATURE [Part::Cylinder] Cylinder2758  label="Válec2728"
  Angle = 360
  AttacherType = Attacher::AttachEngine3D
  Height = 20
  Placement = pos=(-23,0,8) rot=(0,0,1;1.5708rad)
  Radius = 1
FEATURE [Part::Cylinder] Cylinder2759  label="Válec2729"
  Angle = 360
  AttacherType = Attacher::AttachEngine3D
  Height = 20
  Placement = pos=(-16.26,-16.26,8) rot=(0,0,1;2.35619rad)
  Radius = 1
FEATURE [Part::Cylinder] Cylinder2760  label="Válec2730"
  Angle = 360
  AttacherType = Attacher::AttachEngine3D
  Height = 20
  Placement = pos=(4e-15,-23,8) rot=(0,0,1;3.14159rad)
  Radius = 1
FEATURE [Part::Cylinder] Cylinder2761  label="Válec2731"
  Angle = 360
  AttacherType = Attacher::AttachEngine3D
  Height = 20
  Placement = pos=(16.26,-16.26,8) rot=(0,0,1;3.92699rad)
  Radius = 1
FEATURE [Part::Cylinder] Cylinder2762  label="Válec2732"
  Angle = 360
  AttacherType = Attacher::AttachEngine3D
  Height = 20
  Placement = pos=(23,1.1e-14,8) rot=(0,0,-1;1.5708rad)
  Radius = 1
FEATURE [Part::Cylinder] Cylinder2763  label="Válec2733"
  Angle = 360
  AttacherType = Attacher::AttachEngine3D
  Height = 20
  Placement = pos=(16.26,16.26,8) rot=(0,0,-1;0.785398rad)
  Radius = 1
FEATURE [Part::Box] Box952  label="Krychle951"
  AttacherType = Attacher::AttachEngine3D
  Height = 1.4
  Length = 4
  Placement = pos=(-2,21,14) rot=(0,0,1;0rad)
  Width = 4
FEATURE [Part::Box] Box953  label="Krychle952"
  AttacherType = Attacher::AttachEngine3D
  Height = 1.4
  Length = 4
  Placement = pos=(-16.2635,13.435,14) rot=(0,0,1;0.785398rad)
  Width = 4
FEATURE [Part::Box] Box954  label="Krychle953"
  AttacherType = Attacher::AttachEngine3D
  Height = 1.4
  Length = 4
  Placement = pos=(-21,-2,14) rot=(0,0,1;1.5708rad)
  Width = 4
FEATURE [Part::Box] Box955  label="Krychle954"
  AttacherType = Attacher::AttachEngine3D
  Height = 1.4
  Length = 4
  Placement = pos=(-13.435,-16.2635,14) rot=(0,0,1;2.35619rad)
  Width = 4
FEATURE [Part::Box] Box956  label="Krychle955"
  AttacherType = Attacher::AttachEngine3D
  Height = 1.4
  Length = 4
  Placement = pos=(2,-21,14) rot=(0,0,1;3.14159rad)
  Width = 4
FEATURE [Part::Box] Box957  label="Krychle956"
  AttacherType = Attacher::AttachEngine3D
  Height = 1.4
  Length = 4
  Placement = pos=(16.2635,-13.435,14) rot=(0,0,1;3.92699rad)
  Width = 4
FEATURE [Part::Box] Box958  label="Krychle957"
  AttacherType = Attacher::AttachEngine3D
  Height = 1.4
  Length = 4
  Placement = pos=(21,2,14) rot=(0,0,-1;1.5708rad)
  Width = 4
FEATURE [Part::Box] Box959  label="Krychle958"
  AttacherType = Attacher::AttachEngine3D
  Height = 1.4
  Length = 4
  Placement = pos=(13.435,16.2635,14) rot=(0,0,-1;0.785398rad)
  Width = 4
FEATURE [Part::Cylinder] Cylinder2764  label="Válec2734"
  Angle = 360
  AttacherType = Attacher::AttachEngine3D
  Height = 10
  Radius = 21
FEATURE [Part::Cylinder] Cylinder2765  label="Válec2735"
  Angle = 360
  AttacherType = Attacher::AttachEngine3D
  Height = 10
  Radius = 21
FEATURE [Part::Box] Box960  label="Krychle959"
  AttacherType = Attacher::AttachEngine3D
  Height = 1.4
  Length = 4
  Placement = pos=(-2,17,-13) rot=(0,0,1;0rad)
  Width = 4
FEATURE [Part::Box] Box961  label="Krychle960"
  AttacherType = Attacher::AttachEngine3D
  Height = 1.4
  Length = 4
  Placement = pos=(-13.435,10.6066,-13) rot=(0,0,1;0.785398rad)
  Width = 4
FEATURE [Part::Box] Box962  label="Krychle961"
  AttacherType = Attacher::AttachEngine3D
  Height = 1.4
  Length = 4
  Placement = pos=(-10.6066,-13.435,-13) rot=(0,0,1;2.35619rad)
  Width = 4
FEATURE [Part::Box] Box963  label="Krychle962"
  AttacherType = Attacher::AttachEngine3D
  Height = 1.4
  Length = 4
  Placement = pos=(2,-17,-13) rot=(0,0,1;3.14159rad)
  Width = 4
FEATURE [Part::Cylinder] Cylinder2766  label="Válec2736"
  Angle = 360
  AttacherType = Attacher::AttachEngine3D
  Height = 10
  Placement = pos=(0,19,-20) rot=(0,0,1;0rad)
  Radius = 1
FEATURE [Part::Box] Box964  label="Krychle963"
  AttacherType = Attacher::AttachEngine3D
  Height = 1.4
  Length = 4
  Placement = pos=(-17,-2,-13) rot=(0,0,1;1.5708rad)
  Width = 4
FEATURE [Part::Box] Box965  label="Krychle964"
  AttacherType = Attacher::AttachEngine3D
  Height = 1.4
  Length = 4
  Placement = pos=(13.435,-10.6066,-13) rot=(0,0,1;3.92699rad)
  Width = 4
FEATURE [Part::Box] Box966  label="Krychle965"
  AttacherType = Attacher::AttachEngine3D
  Height = 1.4
  Length = 4
  Placement = pos=(10.6066,13.435,-13) rot=(0,0,-1;0.785398rad)
  Width = 4
FEATURE [Part::Cylinder] Cylinder2767  label="Válec2737"
  Angle = 360
  AttacherType = Attacher::AttachEngine3D
  Height = 10
  Placement = pos=(-13.435,13.435,-20) rot=(0,0,1;0.785398rad)
  Radius = 1
FEATURE [Part::Cylinder] Cylinder2768  label="Válec2738"
  Angle = 360
  AttacherType = Attacher::AttachEngine3D
  Height = 10
  Placement = pos=(-19,-1e-15,-20) rot=(0,0,1;1.5708rad)
  Radius = 1
FEATURE [Part::Cylinder] Cylinder2769  label="Válec2739"
  Angle = 360
  AttacherType = Attacher::AttachEngine3D
  Height = 10
  Placement = pos=(-13.435,-13.435,-20) rot=(0,0,1;2.35619rad)
  Radius = 1
FEATURE [Part::Cylinder] Cylinder2770  label="Válec2740"
  Angle = 360
  AttacherType = Attacher::AttachEngine3D
  Height = 10
  Placement = pos=(6e-15,-19,-20) rot=(0,0,1;3.14159rad)
  Radius = 1
FEATURE [Part::Cylinder] Cylinder2771  label="Válec2741"
  Angle = 360
  AttacherType = Attacher::AttachEngine3D
  Height = 10
  Placement = pos=(13.435,-13.435,-20) rot=(0,0,1;3.92699rad)
  Radius = 1
FEATURE [Part::Box] Box967  label="Krychle966"
  AttacherType = Attacher::AttachEngine3D
  Height = 1.4
  Length = 4
  Placement = pos=(17,2,-13) rot=(0,0,-1;1.5708rad)
  Width = 4
FEATURE [Part::Cylinder] Cylinder2772  label="Válec2742"
  Angle = 360
  AttacherType = Attacher::AttachEngine3D
  Height = 10
  Placement = pos=(19,8e-15,-20) rot=(0,0,-1;1.5708rad)
  Radius = 1
FEATURE [Part::Cylinder] Cylinder2773  label="Válec2743"
  Angle = 360
  AttacherType = Attacher::AttachEngine3D
  Height = 10
  Placement = pos=(13.435,13.435,-20) rot=(0,0,-1;0.785398rad)
  Radius = 1
FEATURE [Part::Cylinder] Cylinder2774  label="Válec2744"
  Angle = 360
  AttacherType = Attacher::AttachEngine3D
  Height = 10
  Placement = pos=(0,23,4) rot=(0,0,1;0rad)
  Radius = 1
FEATURE [Part::Cylinder] Cylinder2775  label="Válec2745"
  Angle = 360
  AttacherType = Attacher::AttachEngine3D
  Height = 10
  Placement = pos=(16.2635,16.2635,4) rot=(0,0,-1;0.785398rad)
  Radius = 1
FEATURE [Part::Compound] Compound1233
  Links = -> [Cylinder2756,Cylinder2763,Cylinder2762,Cylinder2760,Cylinder2761,Cylinder2759,Cylinder2757,Cylinder2758]
  Placement = pos=(0,0,-12) rot=(0,0,1;0rad)
FEATURE [Part::Compound] Compound1234
  Links = -> [Box952,Box953,Box954,Box955,Box956,Box957,Box958,Box959]
  Placement = pos=(0,0,-1) rot=(0,0,1;0rad)
FEATURE [Part::Compound] Compound1236
  Links = -> [Box960,Box961,Box964,Box962,Box963,Box965,Box967,Box966]
FEATURE [Part::Compound] Compound1237
  Links = -> [Cylinder2766,Cylinder2767,Cylinder2768,Cylinder2769,Cylinder2770,Cylinder2771,Cylinder2772,Cylinder2773]
FEATURE [Part::Torus] Torus006  label="Anuloid006"
  Angle1 = -180
  Angle2 = 180
  Angle3 = 360
  AttacherType = Attacher::AttachEngine3D
  Placement = pos=(0,0,17.5) rot=(0,0,1;0rad)
  Radius1 = 20
  Radius2 = 2.2
FEATURE [Part::FeaturePython] Tube134  # WARN: FeaturePython — macro-defined, semantics opaque (R4)
  AttacherType = Attacher::AttachEngine3D
  Height = 14
  InnerRadius = 21
  OuterRadius = 25
  Placement = pos=(0,0,10) rot=(0,0,1;0rad)
FEATURE [Part::Cut] Cut1040
  Base = -> Tube134
  Tool = -> Torus006
FEATURE [Part::Cut] Cut1039
  Base = -> Cut1040
  Tool = -> Compound1234
FEATURE [Part::Cut] Cut1038
  Base = -> Cut1039
  Tool = -> Compound1233
FEATURE [Part::Cut] Cut1041
  Base = -> Cut1038
  Tool = -> Cylinder2755
FEATURE [Part::FeaturePython] wormgear045  # WARN: FeaturePython — macro-defined, semantics opaque (R4)
  AttacherType = Attacher::AttachEngine3D
  Placement = pos=(0,0,0) rot=(0,0,1;1.13446rad)
  beta = 42.7094
  clearance = 0.25
  diameter = 32.5
  head = 0
  height = 12
  module = 1
  pressure_angle = 20
  reverse_pitch = true
  teeth = 30
  version = 0.0.3
FEATURE [Part::Cut] Cut1042
  Base = -> Cylinder2764
  Tool = -> wormgear045
FEATURE [Part::FeaturePython] wormgear046  # WARN: FeaturePython — macro-defined, semantics opaque (R4)
  AttacherType = Attacher::AttachEngine3D
  Placement = pos=(0,0,0) rot=(0,0,1;1.09607rad)
  beta = 42.7094
  clearance = 0.25
  diameter = 32.5
  head = 0
  height = 12
  module = 1
  pressure_angle = 20
  reverse_pitch = false
  teeth = 30
  version = 0.0.3
FEATURE [Part::Cut] Cut1043
  Base = -> Cylinder2765
  Placement = pos=(0,0,-10) rot=(0,0,1;0rad)
  Tool = -> wormgear046
FEATURE [Part::Compound] Compound1235  label="gearovina-mini_okruh004"
  Links = -> [Cut1043,Cut1042]
FEATURE [Part::FeaturePython] Tube135  # WARN: FeaturePython — macro-defined, semantics opaque (R4)
  AttacherType = Attacher::AttachEngine3D
  Height = 6
  InnerRadius = 17
  OuterRadius = 21
  Placement = pos=(0,0,-16) rot=(0,0,1;0rad)
FEATURE [Part::Cut] Cut1044
  Base = -> Tube135
  Tool = -> Compound1236
FEATURE [Part::Cut] Cut1045
  Base = -> Cut1044
  Tool = -> Compound1237
FEATURE [Part::FeaturePython] Tube136  # WARN: FeaturePython — macro-defined, semantics opaque (R4)
  AttacherType = Attacher::AttachEngine3D
  Height = 6
  InnerRadius = 20
  OuterRadius = 25
  Placement = pos=(0,0,4) rot=(0,0,1;0rad)
FEATURE [Part::Cylinder] Cylinder2776  label="Válec2746"
  Angle = 360
  AttacherType = Attacher::AttachEngine3D
  Height = 10
  Placement = pos=(16.2635,-16.2635,4) rot=(0,0,1;3.92699rad)
  Radius = 1
FEATURE [Part::Cylinder] Cylinder2777  label="Válec2747"
  Angle = 360
  AttacherType = Attacher::AttachEngine3D
  Height = 10
  Placement = pos=(-16.2635,16.2635,4) rot=(0,0,1;0.785398rad)
  Radius = 1
FEATURE [Part::Cylinder] Cylinder2778  label="Válec2748"
  Angle = 360
  AttacherType = Attacher::AttachEngine3D
  Height = 2
  Placement = pos=(-16.2635,-16.2635,4) rot=(0,0,1;2.35619rad)
  Radius = 2
FEATURE [Part::Cylinder] Cylinder2779  label="Válec2749"
  Angle = 360
  AttacherType = Attacher::AttachEngine3D
  Height = 10
  Placement = pos=(-23,-1e-15,4) rot=(0,0,1;1.5708rad)
  Radius = 1
FEATURE [Part::Cylinder] Cylinder2780  label="Válec2750"
  Angle = 360
  AttacherType = Attacher::AttachEngine3D
  Height = 10
  Placement = pos=(-16.2635,-16.2635,4) rot=(0,0,1;2.35619rad)
  Radius = 1
FEATURE [Part::Cylinder] Cylinder2781  label="Válec2751"
  Angle = 360
  AttacherType = Attacher::AttachEngine3D
  Height = 2
  Placement = pos=(0,23,4) rot=(0,0,1;0rad)
  Radius = 2
FEATURE [Part::Cylinder] Cylinder2782  label="Válec2752"
  Angle = 360
  AttacherType = Attacher::AttachEngine3D
  Height = 10
  Placement = pos=(23,1.1e-14,4) rot=(0,0,-1;1.5708rad)
  Radius = 1
FEATURE [Part::Cylinder] Cylinder2783  label="Válec2753"
  Angle = 360
  AttacherType = Attacher::AttachEngine3D
  Height = 2
  Placement = pos=(-23,-1e-15,4) rot=(0,0,1;1.5708rad)
  Radius = 2
FEATURE [Part::Cylinder] Cylinder2784  label="Válec2754"
  Angle = 360
  AttacherType = Attacher::AttachEngine3D
  Height = 10
  Placement = pos=(4e-15,-23,4) rot=(0,0,1;3.14159rad)
  Radius = 1
FEATURE [Part::Compound] Compound1238
  Links = -> [Cylinder2774,Cylinder2777,Cylinder2779,Cylinder2780,Cylinder2784,Cylinder2776,Cylinder2782,Cylinder2775]
FEATURE [Part::Cylinder] Cylinder2785  label="Válec2755"
  Angle = 360
  AttacherType = Attacher::AttachEngine3D
  Height = 2
  Placement = pos=(16.2635,-16.2635,4) rot=(0,0,1;3.92699rad)
  Radius = 2
FEATURE [Part::Cylinder] Cylinder2786  label="Válec2756"
  Angle = 360
  AttacherType = Attacher::AttachEngine3D
  Height = 2
  Placement = pos=(23,1.1e-14,4) rot=(0,0,-1;1.5708rad)
  Radius = 2
FEATURE [Part::Cylinder] Cylinder2787  label="Válec2757"
  Angle = 360
  AttacherType = Attacher::AttachEngine3D
  Height = 2
  Placement = pos=(16.2635,16.2635,4) rot=(0,0,-1;0.785398rad)
  Radius = 2
FEATURE [Part::Cylinder] Cylinder2788  label="Válec2758"
  Angle = 360
  AttacherType = Attacher::AttachEngine3D
  Height = 2
  Placement = pos=(-16.2635,16.2635,4) rot=(0,0,1;0.785398rad)
  Radius = 2
FEATURE [Part::Cylinder] Cylinder2789  label="Válec2759"
  Angle = 360
  AttacherType = Attacher::AttachEngine3D
  Height = 2
  Placement = pos=(4e-15,-23,4) rot=(0,0,1;3.14159rad)
  Radius = 2
FEATURE [Part::Compound] Compound1239
  Links = -> [Cylinder2781,Cylinder2788,Cylinder2783,Cylinder2778,Cylinder2789,Cylinder2785,Cylinder2786,Cylinder2787]
FEATURE [Part::Cut] Cut1047
  Base = -> Tube136
  Tool = -> Compound1239
FEATURE [Part::Cut] Cut1046
  Base = -> Cut1047
  Tool = -> Compound1238
FEATURE [Part::Compound] Compound1240
  Links = -> [Cut1045,Compound1235,Cut1046]
FEATURE [Part::Compound] Compound1241
  Links = -> [Compound1240,Cut1041]
  Placement = pos=(0,1,37) rot=(1,0,0;1.5708rad)
FEATURE [Part::Box] Box891  label="Krychle890"
  AttacherType = Attacher::AttachEngine3D
  Height = 18
  Length = 30
  Placement = pos=(-15,-17,11) rot=(0,0,1;0rad)
  Width = 64
FEATURE [Part::Box] Box968  label="Krychle967"
  AttacherType = Attacher::AttachEngine3D
  Height = 6
  Length = 2
  Placement = pos=(10,-4,10) rot=(0,0,1;0rad)
  Width = 6
FEATURE [Part::Box] Box969  label="Krychle968"
  AttacherType = Attacher::AttachEngine3D
  Height = 6
  Length = 2
  Placement = pos=(-12,-4,10) rot=(0,0,1;0rad)
  Width = 6
FEATURE [Part::Box] Box970  label="Krychle969"
  AttacherType = Attacher::AttachEngine3D
  Height = 6
  Length = 2
  Placement = pos=(10,26,10) rot=(0,0,1;0rad)
  Width = 6
FEATURE [Part::Box] Box971  label="Krychle970"
  AttacherType = Attacher::AttachEngine3D
  Height = 6
  Length = 2
  Placement = pos=(-12,26,10) rot=(0,0,1;0rad)
  Width = 6
FEATURE [Part::Box] Box972  label="Krychle971"
  AttacherType = Attacher::AttachEngine3D
  Height = 6
  Length = 2
  Placement = pos=(10,12,10) rot=(0,0,1;0rad)
  Width = 6
FEATURE [Part::FeaturePython] Tube123  # WARN: FeaturePython — macro-defined, semantics opaque (R4)
  AttacherType = Attacher::AttachEngine3D
  Height = 64
  InnerRadius = 2
  OuterRadius = 21
  Placement = pos=(0,61,37) rot=(1,0,0;1.5708rad)
FEATURE [Part::FeaturePython] Tube124  # WARN: FeaturePython — macro-defined, semantics opaque (R4)
  AttacherType = Attacher::AttachEngine3D
  Height = 26
  InnerRadius = 2
  OuterRadius = 25
  Placement = pos=(0,-3,37) rot=(1,0,0;1.5708rad)
FEATURE [Part::Cut] Cut977
  Base = -> Box891
  Tool = -> Tube124
FEATURE [Part::Cut] Cut001
  Base = -> Cut977
  Tool = -> Tube123
FEATURE [Part::Box] Box973  label="Krychle972"
  AttacherType = Attacher::AttachEngine3D
  Height = 6
  Length = 2
  Placement = pos=(-12,12,10) rot=(0,0,1;0rad)
  Width = 6
FEATURE [Part::Compound] Compound1242
  Links = -> [Box968,Box969,Box970,Box971,Box972,Box973]
FEATURE [Part::Cut] Cut1048
  Base = -> Cut001
  Tool = -> Compound1242
FEATURE [Part::Cylinder] Cylinder2790  label="Válec2760"
  Angle = 360
  AttacherType = Attacher::AttachEngine3D
  Height = 30
  Radius = 38
FEATURE [Part::Common] Common
  Base = -> Cut1048
  Tool = -> Cylinder2790
FEATURE [Part::Box] Box974  label="Krychle973"
  AttacherType = Attacher::AttachEngine3D
  Height = 18
  Length = 30
  Placement = pos=(-15,-17,11) rot=(0,0,1;0rad)
  Width = 8
FEATURE [Part::FeaturePython] Tube137  # WARN: FeaturePython — macro-defined, semantics opaque (R4)
  AttacherType = Attacher::AttachEngine3D
  Height = 64
  InnerRadius = 2
  OuterRadius = 21
  Placement = pos=(0,61,37) rot=(1,0,0;1.5708rad)
FEATURE [Part::FeaturePython] Tube138  # WARN: FeaturePython — macro-defined, semantics opaque (R4)
  AttacherType = Attacher::AttachEngine3D
  Height = 26
  InnerRadius = 2
  OuterRadius = 25
  Placement = pos=(0,-3,37) rot=(1,0,0;1.5708rad)
FEATURE [Part::Box] Box975  label="Krychle974"
  AttacherType = Attacher::AttachEngine3D
  Height = 6
  Length = 2
  Placement = pos=(-12,-4,10) rot=(0,0,1;0rad)
  Width = 6
FEATURE [Part::Box] Box976  label="Krychle975"
  AttacherType = Attacher::AttachEngine3D
  Height = 6
  Length = 2
  Placement = pos=(10,26,10) rot=(0,0,1;0rad)
  Width = 6
FEATURE [Part::Box] Box977  label="Krychle976"
  AttacherType = Attacher::AttachEngine3D
  Height = 6
  Length = 2
  Placement = pos=(-12,26,10) rot=(0,0,1;0rad)
  Width = 6
FEATURE [Part::Box] Box978  label="Krychle977"
  AttacherType = Attacher::AttachEngine3D
  Height = 6
  Length = 2
  Placement = pos=(10,12,10) rot=(0,0,1;0rad)
  Width = 6
FEATURE [Part::Box] Box979  label="Krychle978"
  AttacherType = Attacher::AttachEngine3D
  Height = 6
  Length = 2
  Placement = pos=(-12,12,10) rot=(0,0,1;0rad)
  Width = 6
FEATURE [Part::Cylinder] Cylinder2791  label="Válec2761"
  Angle = 360
  AttacherType = Attacher::AttachEngine3D
  Height = 30
  Radius = 38
FEATURE [Part::Box] Box980  label="Krychle979"
  AttacherType = Attacher::AttachEngine3D
  Height = 18
  Length = 30
  Placement = pos=(-15,-17,11) rot=(0,0,1;0rad)
  Width = 64
FEATURE [Part::Cut] Cut1049
  Base = -> Box980
  Tool = -> Tube138
FEATURE [Part::Cut] Cut1050
  Base = -> Cut1049
  Tool = -> Tube137
FEATURE [Part::Box] Box981  label="Krychle980"
  AttacherType = Attacher::AttachEngine3D
  Height = 6
  Length = 2
  Placement = pos=(10,-4,10) rot=(0,0,1;0rad)
  Width = 6
FEATURE [Part::Compound] Compound1243
  Links = -> [Box981,Box975,Box976,Box977,Box978,Box979]
FEATURE [Part::Cut] Cut1051
  Base = -> Cut1050
  Tool = -> Compound1243
FEATURE [Part::Common] Common007
  Base = -> Cut1051
  Tool = -> Cylinder2791
FEATURE [Part::Common] Common008
  Base = -> Box974
  Tool = -> Common007
FEATURE [Part::Cylinder] Cylinder2792  label="Válec2762"
  Angle = 360
  AttacherType = Attacher::AttachEngine3D
  Height = 64
  Placement = pos=(-26,-13,14) rot=(0,1,0;1.5708rad)
  Radius = 1.5
FEATURE [Part::Cut] Cut1052
  Base = -> Common008
  Tool = -> Cylinder2792
FEATURE [Part::Box] Box982  label="Krychle981"
  AttacherType = Attacher::AttachEngine3D
  Height = 18
  Length = 30
  Placement = pos=(-15,-9,11) rot=(0,0,1;0rad)
  Width = 26
FEATURE [Part::FeaturePython] Tube139  # WARN: FeaturePython — macro-defined, semantics opaque (R4)
  AttacherType = Attacher::AttachEngine3D
  Height = 64
  InnerRadius = 2
  OuterRadius = 21
  Placement = pos=(0,61,37) rot=(1,0,0;1.5708rad)
FEATURE [Part::FeaturePython] Tube140  # WARN: FeaturePython — macro-defined, semantics opaque (R4)
  AttacherType = Attacher::AttachEngine3D
  Height = 26
  InnerRadius = 2
  OuterRadius = 25
  Placement = pos=(0,-3,37) rot=(1,0,0;1.5708rad)
FEATURE [Part::Box] Box983  label="Krychle982"
  AttacherType = Attacher::AttachEngine3D
  Height = 6
  Length = 2
  Placement = pos=(-12,-4,10) rot=(0,0,1;0rad)
  Width = 6
FEATURE [Part::Box] Box984  label="Krychle983"
  AttacherType = Attacher::AttachEngine3D
  Height = 6
  Length = 2
  Placement = pos=(10,26,10) rot=(0,0,1;0rad)
  Width = 6
FEATURE [Part::Box] Box985  label="Krychle984"
  AttacherType = Attacher::AttachEngine3D
  Height = 6
  Length = 2
  Placement = pos=(-12,26,10) rot=(0,0,1;0rad)
  Width = 6
FEATURE [Part::Box] Box986  label="Krychle985"
  AttacherType = Attacher::AttachEngine3D
  Height = 6
  Length = 2
  Placement = pos=(10,12,10) rot=(0,0,1;0rad)
  Width = 6
FEATURE [Part::Box] Box987  label="Krychle986"
  AttacherType = Attacher::AttachEngine3D
  Height = 6
  Length = 2
  Placement = pos=(-12,12,10) rot=(0,0,1;0rad)
  Width = 6
FEATURE [Part::Cylinder] Cylinder2793  label="Válec2763"
  Angle = 360
  AttacherType = Attacher::AttachEngine3D
  Height = 30
  Radius = 38
FEATURE [Part::Box] Box988  label="Krychle987"
  AttacherType = Attacher::AttachEngine3D
  Height = 18
  Length = 30
  Placement = pos=(-15,-17,11) rot=(0,0,1;0rad)
  Width = 64
FEATURE [Part::Cut] Cut1053
  Base = -> Box988
  Tool = -> Tube140
FEATURE [Part::Cut] Cut1054
  Base = -> Cut1053
  Tool = -> Tube139
FEATURE [Part::Box] Box989  label="Krychle988"
  AttacherType = Attacher::AttachEngine3D
  Height = 6
  Length = 2
  Placement = pos=(10,-4,10) rot=(0,0,1;0rad)
  Width = 6
FEATURE [Part::Compound] Compound1244
  Links = -> [Box989,Box983,Box984,Box985,Box986,Box987]
FEATURE [Part::Cut] Cut1055
  Base = -> Cut1054
  Tool = -> Compound1244
FEATURE [Part::Common] Common009
  Base = -> Cut1055
  Tool = -> Cylinder2793
FEATURE [Part::Common] Common010
  Base = -> Box982
  Tool = -> Common009
FEATURE [Part::Cylinder] Cylinder2794  label="Válec2764"
  Angle = 360
  AttacherType = Attacher::AttachEngine3D
  Height = 64
  Placement = pos=(-26,-1,14) rot=(0,1,0;1.5708rad)
  Radius = 1.5
FEATURE [Part::Cylinder] Cylinder2795  label="Válec2765"
  Angle = 360
  AttacherType = Attacher::AttachEngine3D
  Height = 64
  Placement = pos=(-26,12,14) rot=(0,1,0;1.5708rad)
  Radius = 1.5
FEATURE [Part::Compound] Compound1245
  Links = -> [Cylinder2794,Cylinder2795]
FEATURE [Part::Cut] Cut1056
  Base = -> Common010
  Tool = -> Compound1245
FEATURE [Part::FeaturePython] Tube032  # WARN: FeaturePython — macro-defined, semantics opaque (R4)
  AttacherType = Attacher::AttachEngine3D
  Height = 6
  InnerRadius = 17
  OuterRadius = 21
  Placement = pos=(0,0,-22) rot=(0,0,1;0rad)
FEATURE [Part::Box] Box055  label="Krychle055"
  AttacherType = Attacher::AttachEngine3D
  Height = 4
  Length = 46.3
  Placement = pos=(-23.15,-23.15,-25) rot=(0,0,1;0rad)
  Width = 46.3
FEATURE [Part::Cylinder] Cylinder168  label="Válec168"
  Angle = 360
  AttacherType = Attacher::AttachEngine3D
  Height = 10
  Placement = pos=(-13.44,13.44,-24) rot=(0,0,1;0.785398rad)
  Radius = 1
FEATURE [Part::Cylinder] Cylinder169  label="Válec169"
  Angle = 360
  AttacherType = Attacher::AttachEngine3D
  Height = 10
  Placement = pos=(-19,0,-24) rot=(0,0,1;1.5708rad)
  Radius = 1
FEATURE [Part::Cylinder] Cylinder170  label="Válec170"
  Angle = 360
  AttacherType = Attacher::AttachEngine3D
  Height = 10
  Placement = pos=(0,19,-24) rot=(0,0,1;0rad)
  Radius = 1
FEATURE [Part::Cylinder] Cylinder171  label="Válec171"
  Angle = 360
  AttacherType = Attacher::AttachEngine3D
  Height = 10
  Placement = pos=(-13.44,-13.44,-24) rot=(0,0,1;2.35619rad)
  Radius = 1
FEATURE [Part::Cylinder] Cylinder172  label="Válec172"
  Angle = 360
  AttacherType = Attacher::AttachEngine3D
  Height = 10
  Placement = pos=(6e-15,-19,-24) rot=(0,0,1;3.14159rad)
  Radius = 1
FEATURE [Part::Cylinder] Cylinder173  label="Válec173"
  Angle = 360
  AttacherType = Attacher::AttachEngine3D
  Height = 10
  Placement = pos=(13.44,-13.44,-24) rot=(0,0,1;3.92699rad)
  Radius = 1
FEATURE [Part::Cylinder] Cylinder174  label="Válec174"
  Angle = 360
  AttacherType = Attacher::AttachEngine3D
  Height = 10
  Placement = pos=(19,8e-15,-24) rot=(0,0,-1;1.5708rad)
  Radius = 1
FEATURE [Part::Cylinder] Cylinder175  label="Válec175"
  Angle = 360
  AttacherType = Attacher::AttachEngine3D
  Height = 10
  Placement = pos=(13.44,13.44,-24) rot=(0,0,-1;0.785398rad)
  Radius = 1
FEATURE [Part::Cylinder] Cylinder176  label="Válec176"
  Angle = 360
  AttacherType = Attacher::AttachEngine3D
  Height = 2
  Placement = pos=(-19,0,-22) rot=(0,0,1;1.5708rad)
  Radius = 2
FEATURE [Part::Cylinder] Cylinder177  label="Válec177"
  Angle = 360
  AttacherType = Attacher::AttachEngine3D
  Height = 2
  Placement = pos=(6e-15,-19,-22) rot=(0,0,1;3.14159rad)
  Radius = 2
FEATURE [Part::Compound] Compound062
  Links = -> [Cylinder170,Cylinder168,Cylinder169,Cylinder171,Cylinder172,Cylinder173,Cylinder174,Cylinder175]
FEATURE [Part::Cylinder] Cylinder178  label="Válec178"
  Angle = 360
  AttacherType = Attacher::AttachEngine3D
  Height = 2
  Placement = pos=(0,19,-22) rot=(0,0,1;0rad)
  Radius = 2
FEATURE [Part::Cylinder] Cylinder179  label="Válec179"
  Angle = 360
  AttacherType = Attacher::AttachEngine3D
  Height = 2
  Placement = pos=(-13.44,13.44,-22) rot=(0,0,1;0.785398rad)
  Radius = 2
FEATURE [Part::Cylinder] Cylinder180  label="Válec180"
  Angle = 360
  AttacherType = Attacher::AttachEngine3D
  Height = 2
  Placement = pos=(-13.44,-13.44,-22) rot=(0,0,1;2.35619rad)
  Radius = 2
FEATURE [Part::Cylinder] Cylinder181  label="Válec181"
  Angle = 360
  AttacherType = Attacher::AttachEngine3D
  Height = 2
  Placement = pos=(19,8e-15,-22) rot=(0,0,-1;1.5708rad)
  Radius = 2
FEATURE [Part::Cylinder] Cylinder182  label="Válec182"
  Angle = 360
  AttacherType = Attacher::AttachEngine3D
  Height = 2
  Placement = pos=(13.44,-13.44,-22) rot=(0,0,1;3.92699rad)
  Radius = 2
FEATURE [Part::Cylinder] Cylinder183  label="Válec183"
  Angle = 360
  AttacherType = Attacher::AttachEngine3D
  Height = 2
  Placement = pos=(13.44,13.44,-22) rot=(0,0,-1;0.785398rad)
  Radius = 2
FEATURE [Part::Compound] Compound063
  Links = -> [Cylinder178,Cylinder179,Cylinder176,Cylinder180,Cylinder177,Cylinder182,Cylinder181,Cylinder183]
  Placement = pos=(0,0,-3) rot=(0,0,1;0rad)
FEATURE [Part::Cut] Cut062
  Base = -> Box055
  Tool = -> Compound063
FEATURE [Part::Cut] Cut064
  Base = -> Cut062
  Tool = -> Compound062
FEATURE [Part::Cylinder] Cylinder184  label="Válec184"
  Angle = 360
  AttacherType = Attacher::AttachEngine3D
  Height = 10
  Placement = pos=(-19,0,-24) rot=(0,0,1;1.5708rad)
  Radius = 1
FEATURE [Part::Cylinder] Cylinder185  label="Válec185"
  Angle = 360
  AttacherType = Attacher::AttachEngine3D
  Height = 10
  Placement = pos=(6e-15,-19,-24) rot=(0,0,1;3.14159rad)
  Radius = 1
FEATURE [Part::Cylinder] Cylinder186  label="Válec186"
  Angle = 360
  AttacherType = Attacher::AttachEngine3D
  Height = 10
  Placement = pos=(0,19,-24) rot=(0,0,1;0rad)
  Radius = 1
FEATURE [Part::Cylinder] Cylinder187  label="Válec187"
  Angle = 360
  AttacherType = Attacher::AttachEngine3D
  Height = 10
  Placement = pos=(-13.44,13.44,-24) rot=(0,0,1;0.785398rad)
  Radius = 1
FEATURE [Part::Cylinder] Cylinder188  label="Válec188"
  Angle = 360
  AttacherType = Attacher::AttachEngine3D
  Height = 10
  Placement = pos=(-13.44,-13.44,-24) rot=(0,0,1;2.35619rad)
  Radius = 1
FEATURE [Part::Cylinder] Cylinder189  label="Válec189"
  Angle = 360
  AttacherType = Attacher::AttachEngine3D
  Height = 10
  Placement = pos=(19,8e-15,-24) rot=(0,0,-1;1.5708rad)
  Radius = 1
FEATURE [Part::Cylinder] Cylinder190  label="Válec190"
  Angle = 360
  AttacherType = Attacher::AttachEngine3D
  Height = 10
  Placement = pos=(13.44,-13.44,-24) rot=(0,0,1;3.92699rad)
  Radius = 1
FEATURE [Part::Cylinder] Cylinder191  label="Válec191"
  Angle = 360
  AttacherType = Attacher::AttachEngine3D
  Height = 10
  Placement = pos=(13.44,13.44,-24) rot=(0,0,-1;0.785398rad)
  Radius = 1
FEATURE [Part::Compound] Compound066
  Links = -> [Cylinder186,Cylinder187,Cylinder184,Cylinder188,Cylinder185,Cylinder190,Cylinder189,Cylinder191]
FEATURE [Part::Cut] Cut063
  Base = -> Tube032
  Tool = -> Compound066
FEATURE [Part::Cylinder] Cylinder192  label="Válec192"
  Angle = 360
  AttacherType = Attacher::AttachEngine3D
  Height = 50
  Placement = pos=(0,0,-29) rot=(0,0,1;0rad)
  Radius = 8
FEATURE [Part::Cut] Cut065
  Base = -> Cut064
  Tool = -> Cylinder192
FEATURE [Part::Cylinder] Cylinder193  label="Válec193"
  Angle = 360
  AttacherType = Attacher::AttachEngine3D
  Height = 3
  Placement = pos=(-19,-19,-24) rot=(0,0,1;0rad)
  Radius = 3
FEATURE [Part::Cylinder] Cylinder194  label="Válec194"
  Angle = 360
  AttacherType = Attacher::AttachEngine3D
  Height = 10
  Placement = pos=(-19.5,-19.5,-28) rot=(0,0,1;0rad)
  Radius = 1.5
FEATURE [Part::Cylinder] Cylinder195  label="Válec195"
  Angle = 360
  AttacherType = Attacher::AttachEngine3D
  Height = 10
  Placement = pos=(-19.5,19.5,-28) rot=(0,0,1;0rad)
  Radius = 1.5
FEATURE [Part::Cylinder] Cylinder196  label="Válec196"
  Angle = 360
  AttacherType = Attacher::AttachEngine3D
  Height = 10
  Placement = pos=(19.5,-19.5,-28) rot=(0,0,1;0rad)
  Radius = 1.5
FEATURE [Part::Cylinder] Cylinder197  label="Válec197"
  Angle = 360
  AttacherType = Attacher::AttachEngine3D
  Height = 10
  Placement = pos=(19.5,19.5,-28) rot=(0,0,1;0rad)
  Radius = 1.5
FEATURE [Part::Compound] Compound067
  Links = -> [Cylinder194,Cylinder195,Cylinder196,Cylinder197]
FEATURE [Part::Cut] Cut066
  Base = -> Cut065
  Tool = -> Compound067
FEATURE [Part::Cylinder] Cylinder198  label="Válec198"
  Angle = 360
  AttacherType = Attacher::AttachEngine3D
  Height = 3
  Placement = pos=(19,-19,-24) rot=(0,0,1;0rad)
  Radius = 3
FEATURE [Part::Cylinder] Cylinder199  label="Válec199"
  Angle = 360
  AttacherType = Attacher::AttachEngine3D
  Height = 3
  Placement = pos=(-19,19,-24) rot=(0,0,1;0rad)
  Radius = 3
FEATURE [Part::Cylinder] Cylinder200  label="Válec200"
  Angle = 360
  AttacherType = Attacher::AttachEngine3D
  Height = 3
  Placement = pos=(19,19,-24) rot=(0,0,1;0rad)
  Radius = 3
FEATURE [Part::Compound] Compound068
  Links = -> [Cylinder193,Cylinder198,Cylinder199,Cylinder200]
  Placement = pos=(0,0,4) rot=(0,0,1;0rad)
FEATURE [Part::Cut] Cut067
  Base = -> Cut066
  Tool = -> Compound068
FEATURE [Part::Compound] Compound069
  Links = -> [Cut067,Cut063]
FEATURE [Part::Chamfer] Chamfer145
  Base = -> Compound069
  Edges = 2 edges r=2: [Edge1,Edge3]
FEATURE [Part::Chamfer] Chamfer001  label="G-mini_moto-holder-A"
  Base = -> Chamfer145
  Edges = 2 edges r=2: [Edge43,Edge44]
  Placement = pos=(0,1,37) rot=(1,0,0;1.5708rad)
FEATURE [Part::Box] Box990  label="Krychle989"
  AttacherType = Attacher::AttachEngine3D
  Height = 18
  Length = 48
  Placement = pos=(-24,22,13.5) rot=(0,0,1;0rad)
  Width = 20
FEATURE [Part::Box] Box991  label="Krychle990"
  AttacherType = Attacher::AttachEngine3D
  Height = 18
  Length = 48
  Placement = pos=(-24,17,11) rot=(0,0,1;0rad)
  Width = 5
FEATURE [Part::FeaturePython] Tube141  # WARN: FeaturePython — macro-defined, semantics opaque (R4)
  AttacherType = Attacher::AttachEngine3D
  Height = 26
  InnerRadius = 2
  OuterRadius = 25
  Placement = pos=(0,-3,37) rot=(1,0,0;1.5708rad)
FEATURE [Part::FeaturePython] Tube142  # WARN: FeaturePython — macro-defined, semantics opaque (R4)
  AttacherType = Attacher::AttachEngine3D
  Height = 64
  InnerRadius = 2
  OuterRadius = 21
  Placement = pos=(0,61,37) rot=(1,0,0;1.5708rad)
FEATURE [Part::Box] Box992  label="Krychle991"
  AttacherType = Attacher::AttachEngine3D
  Height = 6
  Length = 2
  Placement = pos=(10,26,10) rot=(0,0,1;0rad)
  Width = 6
FEATURE [Part::Box] Box993  label="Krychle992"
  AttacherType = Attacher::AttachEngine3D
  Height = 6
  Length = 2
  Placement = pos=(-12,26,10) rot=(0,0,1;0rad)
  Width = 6
FEATURE [Part::Box] Box994  label="Krychle993"
  AttacherType = Attacher::AttachEngine3D
  Height = 6
  Length = 2
  Placement = pos=(10,12,10) rot=(0,0,1;0rad)
  Width = 6
FEATURE [Part::Box] Box995  label="Krychle994"
  AttacherType = Attacher::AttachEngine3D
  Height = 6
  Length = 2
  Placement = pos=(-12,12,10) rot=(0,0,1;0rad)
  Width = 6
FEATURE [Part::Cylinder] Cylinder2796  label="Válec2766"
  Angle = 360
  AttacherType = Attacher::AttachEngine3D
  Height = 30
  Radius = 38
FEATURE [Part::Box] Box996  label="Krychle995"
  AttacherType = Attacher::AttachEngine3D
  Height = 18
  Length = 30
  Placement = pos=(-15,-17,11) rot=(0,0,1;0rad)
  Width = 64
FEATURE [Part::Cut] Cut1057
  Base = -> Box996
  Tool = -> Tube141
FEATURE [Part::Cut] Cut1058
  Base = -> Cut1057
  Tool = -> Tube142
FEATURE [Part::Box] Box997  label="Krychle996"
  AttacherType = Attacher::AttachEngine3D
  Height = 6
  Length = 2
  Placement = pos=(10,-4,10) rot=(0,0,1;0rad)
  Width = 6
FEATURE [Part::Cylinder] Cylinder2797  label="Válec2767"
  Angle = 360
  AttacherType = Attacher::AttachEngine3D
  Height = 64
  Placement = pos=(-26,12,14) rot=(0,1,0;1.5708rad)
  Radius = 1.5
FEATURE [Part::Cylinder] Cylinder2798  label="Válec2768"
  Angle = 360
  AttacherType = Attacher::AttachEngine3D
  Height = 64
  Placement = pos=(-26,-1,14) rot=(0,1,0;1.5708rad)
  Radius = 1.5
FEATURE [Part::Box] Box998  label="Krychle997"
  AttacherType = Attacher::AttachEngine3D
  Height = 18
  Length = 30
  Placement = pos=(-15,-9,11) rot=(0,0,1;0rad)
  Width = 26
FEATURE [Part::Box] Box999  label="Krychle998"
  AttacherType = Attacher::AttachEngine3D
  Height = 6
  Length = 2
  Placement = pos=(-12,-4,10) rot=(0,0,1;0rad)
  Width = 6
FEATURE [Part::Compound] Compound1246
  Links = -> [Box997,Box999,Box992,Box993,Box994,Box995]
FEATURE [Part::Cut] Cut1059
  Base = -> Cut1058
  Tool = -> Compound1246
FEATURE [Part::Common] Common011
  Base = -> Cut1059
  Tool = -> Cylinder2796
FEATURE [Part::Common] Common012
  Base = -> Box998
  Tool = -> Common011
FEATURE [Part::Compound] Compound1247
  Links = -> [Cylinder2798,Cylinder2797]
FEATURE [Part::Cut] Cut1060
  Base = -> Common012
  Placement = pos=(0,5,0) rot=(0,0,1;0rad)
  Tool = -> Compound1247
FEATURE [Part::Cut] Cut1061
  Base = -> Cut1010
  Tool = -> Box990
FEATURE [Part::Compound] Compound1248  label="Wrist_side-actuator2"
  Links = -> [Cut1005,Cut1006,Cut1007,Cut1061]
FEATURE [Part::Compound] Compound1249  label="Wrist_side-actuator-old"
  Links = -> [Tube125,Compound1248]
FEATURE [Part::Box] Box1000  label="Krychle999"
  AttacherType = Attacher::AttachEngine3D
  Height = 9
  Length = 54
  Placement = pos=(-27,70,75) rot=(0,0,1;0rad)
  Width = 58
FEATURE [Part::Cylinder] Cylinder2799  label="Válec2769"
  Angle = 360
  AttacherType = Attacher::AttachEngine3D
  Height = 60
  Placement = pos=(24,73,-80) rot=(0,0,1;0rad)
  Radius = 1.5
FEATURE [Part::Cylinder] Cylinder2800  label="Válec2770"
  Angle = 360
  AttacherType = Attacher::AttachEngine3D
  Height = 60
  Placement = pos=(-24,73,-80) rot=(0,0,1;0rad)
  Radius = 1.5
FEATURE [Part::Cylinder] Cylinder2801  label="Válec2771"
  Angle = 360
  AttacherType = Attacher::AttachEngine3D
  Height = 60
  Placement = pos=(-15,125,-80) rot=(0,0,1;0rad)
  Radius = 1.5
FEATURE [Part::Cylinder] Cylinder2802  label="Válec2772"
  Angle = 360
  AttacherType = Attacher::AttachEngine3D
  Height = 60
  Placement = pos=(15,125,-80) rot=(0,0,1;0rad)
  Radius = 1.5
FEATURE [Part::Compound] Compound1251
  Links = -> [Cylinder2799,Cylinder2800,Cylinder2801,Cylinder2802]
  Placement = pos=(0,0,120) rot=(0,0,1;0rad)
FEATURE [Part::Box] Box1001  label="Krychle1000"
  AttacherType = Attacher::AttachEngine3D
  Height = 50
  Length = 42
  Placement = pos=(-21,76,38) rot=(0,0,1;0rad)
  Width = 46
FEATURE [Part::Box] Box1002  label="Krychle1001"
  AttacherType = Attacher::AttachEngine3D
  Height = 50
  Length = 42
  Placement = pos=(-21,76,38) rot=(0,0,1;0rad)
  Width = 46
FEATURE [Part::Cylinder] Cylinder2803  label="Válec2773"
  Angle = 360
  AttacherType = Attacher::AttachEngine3D
  Height = 3
  Placement = pos=(-24,128,72) rot=(1,0,0;1.5708rad)
  Radius = 3
FEATURE [Part::Box] Box1003  label="Krychle1002"
  AttacherType = Attacher::AttachEngine3D
  Height = 10
  Length = 54
  Placement = pos=(-27,70,75) rot=(0,0,1;0rad)
  Width = 58
FEATURE [Part::Cut] Cut1062
  Base = -> Box1003
  Tool = -> Box1002
FEATURE [Part::Cut] Cut1068
  Base = -> Box1000
  Placement = pos=(0,0,10) rot=(0,0,1;0rad)
  Tool = -> Box1001
FEATURE [Part::Chamfer] Chamfer146
  Base = -> Cut1068
  Edges = 2 edges r=3: [Edge3,Edge15]
FEATURE [Part::Cut] Cut1063
  Base = -> Chamfer146
  Tool = -> Compound1251
FEATURE [Part::Cylinder] Cylinder2804  label="Válec2774"
  Angle = 360
  AttacherType = Attacher::AttachEngine3D
  Height = 60
  Placement = pos=(24,73,-80) rot=(0,0,1;0rad)
  Radius = 1.5
FEATURE [Part::Cylinder] Cylinder2805  label="Válec2775"
  Angle = 360
  AttacherType = Attacher::AttachEngine3D
  Height = 60
  Placement = pos=(-15,125,-80) rot=(0,0,1;0rad)
  Radius = 1.5
FEATURE [Part::Cylinder] Cylinder2806  label="Válec2776"
  Angle = 360
  AttacherType = Attacher::AttachEngine3D
  Height = 3
  Placement = pos=(24,128,72) rot=(1,0,0;1.5708rad)
  Radius = 3
FEATURE [Part::Compound] Compound1250
  Links = -> [Cylinder2803,Cylinder2806]
  Placement = pos=(0,0,8) rot=(0,0,1;0rad)
FEATURE [Part::Cylinder] Cylinder2807  label="Válec2777"
  Angle = 360
  AttacherType = Attacher::AttachEngine3D
  Height = 50
  Placement = pos=(-24,140,72) rot=(1,0,0;1.5708rad)
  Radius = 1.5
FEATURE [Part::Cylinder] Cylinder2808  label="Válec2778"
  Angle = 360
  AttacherType = Attacher::AttachEngine3D
  Height = 60
  Placement = pos=(15,125,-80) rot=(0,0,1;0rad)
  Radius = 1.5
FEATURE [Part::Cylinder] Cylinder2809  label="Válec2779"
  Angle = 360
  AttacherType = Attacher::AttachEngine3D
  Height = 50
  Placement = pos=(24,140,72) rot=(1,0,0;1.5708rad)
  Radius = 1.5
FEATURE [Part::Compound] Compound1252
  Links = -> [Cylinder2807,Cylinder2809]
  Placement = pos=(0,0,8) rot=(0,0,1;0rad)
FEATURE [Part::Box] Box1004  label="Krychle1003"
  AttacherType = Attacher::AttachEngine3D
  Height = 10
  Length = 56
  Placement = pos=(-28,78,75) rot=(0,0,1;0rad)
  Width = 44
FEATURE [Part::Cut] Cut1066
  Base = -> Cut1062
  Tool = -> Box1004
FEATURE [Part::Cylinder] Cylinder2810  label="Válec2780"
  Angle = 360
  AttacherType = Attacher::AttachEngine3D
  Height = 60
  Placement = pos=(-24,73,-80) rot=(0,0,1;0rad)
  Radius = 1.5
FEATURE [Part::Compound] Compound1253
  Links = -> [Cylinder2804,Cylinder2810,Cylinder2805,Cylinder2808]
  Placement = pos=(0,0,120) rot=(0,0,1;0rad)
FEATURE [Part::Cut] Cut1067
  Base = -> Cut1066
  Tool = -> Compound1253
FEATURE [Part::Chamfer] Chamfer147
  Base = -> Cut1067
  Edges = 2 edges r=3: [Edge32,Edge43]
FEATURE [Part::Cut] Cut1064
  Base = -> Chamfer147
  Tool = -> Compound1250
FEATURE [Part::Cut] Cut1065
  Base = -> Cut1064
  Tool = -> Compound1252
FEATURE [Part::Compound] Compound1254  label="G-mini_encoder_front-holder"
  Links = -> [Cut1063,Cut1065]
  Placement = pos=(0,-3,65) rot=(0,0.707107,-0.707107;3.14159rad)
FEATURE [Part::Box] Box646  label="Krychle646"
  AttacherType = Attacher::AttachEngine3D
  Height = 9
  Length = 28.8
  Placement = pos=(-14.4,-14,34) rot=(0,0,1;0rad)
  Width = 34.4
FEATURE [Part::Compound] Compound804
  Links = -> [Box646]
  Placement = pos=(63.64,-63.64,33) rot=(0,0,1;3.92699rad)
FEATURE [Part::Box] Box651  label="Krychle651"
  AttacherType = Attacher::AttachEngine3D
  Height = 9
  Length = 42
  Placement = pos=(-21,-12,34) rot=(0,0,1;0rad)
  Width = 24
FEATURE [Part::Box] Box653  label="Krychle653"
  AttacherType = Attacher::AttachEngine3D
  Height = 1
  Length = 54
  Placement = pos=(-27,-12,34) rot=(0,0,1;0rad)
  Width = 24
FEATURE [Part::Compound] Compound811
  Links = -> [Box653]
  Placement = pos=(63.64,-63.64,42) rot=(0,0,1;3.92699rad)
FEATURE [Part::Cylinder] Cylinder1643  label="Válec1643"
  Angle = 360
  AttacherType = Attacher::AttachEngine3D
  Height = 1
  Placement = pos=(63.64,-63.64,76) rot=(0,0,1;3.92699rad)
  Radius = 4
FEATURE [Part::Cut] Cut470
  Base = -> Compound811
  Tool = -> Cylinder1643
FEATURE [Part::Box] Box659  label="Krychle659"
  AttacherType = Attacher::AttachEngine3D
  Height = 9
  Length = 42
  Placement = pos=(-21,-14,34) rot=(0,0,1;0rad)
  Width = 28
FEATURE [Part::Compound] Compound824
  Links = -> [Box659]
  Placement = pos=(63.64,-63.64,33) rot=(0,0,1;3.92699rad)
FEATURE [Part::Cylinder] Cylinder1681  label="Válec1681"
  Angle = 360
  AttacherType = Attacher::AttachEngine3D
  Height = 60
  Placement = pos=(-18,85,-57) rot=(0,0,1;0rad)
  Radius = 1.5
FEATURE [Part::Cylinder] Cylinder1697  label="Válec1697"
  Angle = 360
  AttacherType = Attacher::AttachEngine3D
  Height = 100
  Placement = pos=(24,110,72) rot=(1,0,0;1.5708rad)
  Radius = 1.5
FEATURE [Part::Compound] Compound840
  Links = -> [Cylinder1697]
  Placement = pos=(0,0,0) rot=(0,0,1;3.92699rad)
FEATURE [Part::Cylinder] Cylinder1621  label="Válec1621"
  Angle = 360
  AttacherType = Attacher::AttachEngine3D
  Height = 60
  Placement = pos=(18,95,-57) rot=(0,0,1;0rad)
  Radius = 1.5
FEATURE [Part::Cylinder] Cylinder1676  label="Válec1676"
  Angle = 360
  AttacherType = Attacher::AttachEngine3D
  Height = 60
  Placement = pos=(-18,95,-57) rot=(0,0,1;0rad)
  Radius = 1.5
FEATURE [Part::Cylinder] Cylinder1683  label="Válec1683"
  Angle = 360
  AttacherType = Attacher::AttachEngine3D
  Height = 60
  Placement = pos=(18,95,-57) rot=(0,0,1;0rad)
  Radius = 1.5
FEATURE [Part::Cylinder] Cylinder1682  label="Válec1682"
  Angle = 360
  AttacherType = Attacher::AttachEngine3D
  Height = 60
  Placement = pos=(-18,95,-57) rot=(0,0,1;0rad)
  Radius = 1.5
FEATURE [Part::Cylinder] Cylinder1670  label="Válec1670"
  Angle = 360
  AttacherType = Attacher::AttachEngine3D
  Height = 20
  Placement = pos=(15.75,114,39.48) rot=(0,0.707107,0.707107;3.14159rad)
  Radius = 1.5
FEATURE [Part::Cylinder] Cylinder1675  label="Válec1675"
  Angle = 360
  AttacherType = Attacher::AttachEngine3D
  Height = 60
  Placement = pos=(-18,85,-57) rot=(0,0,1;0rad)
  Radius = 1.5
FEATURE [Part::Cylinder] Cylinder1671  label="Válec1671"
  Angle = 360
  AttacherType = Attacher::AttachEngine3D
  Height = 20
  Placement = pos=(15.75,114,58.525) rot=(0,0.707107,0.707107;3.14159rad)
  Radius = 1.5
FEATURE [Part::Compound] Compound826
  Links = -> [Cylinder1670,Cylinder1671]
  Placement = pos=(-49,0,-96) rot=(0.57735,0.57735,0.57735;2.0944rad)
FEATURE [Part::Compound] Compound827
  Links = -> [Compound826]
  Placement = pos=(52.33,-52.33,52) rot=(0,0,1;3.92699rad)
FEATURE [Part::Cylinder] Cylinder1772  label="Válec1772"
  Angle = 360
  AttacherType = Attacher::AttachEngine3D
  Height = 100
  Placement = pos=(-24,110,72) rot=(1,0,0;1.5708rad)
  Radius = 1.5
FEATURE [Part::Compound] Compound839
  Links = -> [Cylinder1772]
  Placement = pos=(0,0,0) rot=(0,0,1;3.92699rad)
FEATURE [Part::Box] Box704  label="Krychle704"
  AttacherType = Attacher::AttachEngine3D
  Height = 6
  Length = 6
  Placement = pos=(21,90,69) rot=(0,0,1;0rad)
  Width = 2
FEATURE [Part::Compound] Compound837
  Links = -> [Box704]
  Placement = pos=(0,0,0) rot=(0,0,1;3.92699rad)
FEATURE [Part::Box] Box660  label="Krychle660"
  AttacherType = Attacher::AttachEngine3D
  Height = 9
  Length = 54
  Placement = pos=(-27,-12,34) rot=(0,0,1;0rad)
  Width = 24
FEATURE [Part::Compound] Compound825
  Links = -> [Box660]
  Placement = pos=(63.64,-63.64,33) rot=(0,0,1;3.92699rad)
FEATURE [Part::Cut] Cut475
  Base = -> Compound825
  Tool = -> Compound824
FEATURE [Part::Cylinder] Cylinder1674  label="Válec1674"
  Angle = 360
  AttacherType = Attacher::AttachEngine3D
  Height = 60
  Placement = pos=(18,85,-57) rot=(0,0,1;0rad)
  Radius = 1.5
FEATURE [Part::Compound] Compound806
  Links = -> [Cylinder1621,Cylinder1674,Cylinder1675,Cylinder1676]
  Placement = pos=(0,0,100) rot=(0,0,1;3.92699rad)
FEATURE [Part::Cylinder] Cylinder1684  label="Válec1684"
  Angle = 360
  AttacherType = Attacher::AttachEngine3D
  Height = 60
  Placement = pos=(18,85,-57) rot=(0,0,1;0rad)
  Radius = 1.5
FEATURE [Part::Compound] Compound831
  Links = -> [Cylinder1683,Cylinder1684,Cylinder1681,Cylinder1682]
  Placement = pos=(0,0,100) rot=(0,0,1;3.92699rad)
FEATURE [Part::Box] Box665  label="Krychle665"
  AttacherType = Attacher::AttachEngine3D
  Height = 6
  Length = 6
  Placement = pos=(-27,90,69) rot=(0,0,1;0rad)
  Width = 2
FEATURE [Part::Compound] Compound838
  Links = -> [Box665]
  Placement = pos=(0,0,0) rot=(0,0,1;3.92699rad)
FEATURE [Part::Cut] Cut477
  Base = -> Cut470
  Tool = -> Compound827
FEATURE [Part::Cut] Cut480
  Base = -> Cut477
  Tool = -> Compound831
FEATURE [Part::Compound] Compound842
  Links = -> [Compound839,Compound840]
FEATURE [Part::Compound] Compound809
  Links = -> [Box651]
  Placement = pos=(63.64,-63.64,33) rot=(0,0,1;3.92699rad)
FEATURE [Part::Cut] Cut469
  Base = -> Compound809
  Tool = -> Compound804
FEATURE [Part::Compound] Compound835
  Links = -> [Cut469,Cut475]
FEATURE [Part::Cut] Cut483
  Base = -> Compound835
  Tool = -> Compound806
FEATURE [Part::Compound] Compound836  label="Base_encoder-sidehold2"
  Links = -> [Cut483,Cut480]
FEATURE [Part::Compound] Compound841
  Links = -> [Compound837,Compound838]
FEATURE [Part::Cut] Cut484
  Base = -> Compound836
  Tool = -> Compound841
FEATURE [Part::Cut] Cut485  label="Base_encoder-sidehold004"
  Base = -> Cut484
  Tool = -> Compound842
FEATURE [Part::Chamfer] Chamfer049
  Base = -> Cut485
  Edges = 4 edges r=1: [Edge48,Edge82,Edge99,Edge114]
FEATURE [Part::Chamfer] Chamfer050
  Base = -> Chamfer049
  Edges = 2 edges r=1: [Edge3,Edge68]
FEATURE [Part::Chamfer] Chamfer051  label="G-mini_encoder-sidehold"
  Base = -> Chamfer050
  Edges = 2 edges r=1: [Edge69,Edge97]
  Placement = pos=(0,0,-2) rot=(0,0,1;0rad)
FEATURE [Part::Box] Box656  label="Krychle656"
  AttacherType = Attacher::AttachEngine3D
  Height = 7
  Length = 42
  Placement = pos=(-21,-12,34) rot=(0,0,1;0rad)
  Width = 24
FEATURE [Part::Compound] Compound815
  Links = -> [Box656]
  Placement = pos=(63.64,-63.64,43) rot=(0,0,1;3.92699rad)
FEATURE [Part::FeaturePython] Tube  # WARN: FeaturePython — macro-defined, semantics opaque (R4)
  AttacherType = Attacher::AttachEngine3D
  Height = 1
  InnerRadius = 4
  OuterRadius = 5
  Placement = pos=(0,90,81) rot=(0,0,1;0rad)
FEATURE [Part::Compound] Compound814
  Links = -> [Tube]
  Placement = pos=(0,0,0) rot=(0,0,1;3.92699rad)
FEATURE [Part::Cylinder] Cylinder1644  label="Válec1644"
  Angle = 360
  AttacherType = Attacher::AttachEngine3D
  Height = 5
  Placement = pos=(0,90,77) rot=(0,0,1;0rad)
  Radius = 5
FEATURE [Part::Compound] Compound816
  Links = -> [Cylinder1644]
  Placement = pos=(0,0,0) rot=(0,0,1;3.92699rad)
FEATURE [Part::Cut] Cut471
  Base = -> Compound815
  Tool = -> Compound816
FEATURE [Part::Compound] Compound817
  Links = -> [Compound814,Cut471]
FEATURE [Part::Cylinder] Cylinder1673  label="Válec1673"
  Angle = 360
  AttacherType = Attacher::AttachEngine3D
  Height = 20
  Placement = pos=(15.75,114,58.525) rot=(0,0.707107,0.707107;3.14159rad)
  Radius = 1.5
FEATURE [Part::Cylinder] Cylinder1672  label="Válec1672"
  Angle = 360
  AttacherType = Attacher::AttachEngine3D
  Height = 20
  Placement = pos=(15.75,114,39.48) rot=(0,0.707107,0.707107;3.14159rad)
  Radius = 1.5
FEATURE [Part::Compound] Compound828
  Links = -> [Cylinder1672,Cylinder1673]
  Placement = pos=(-49,0,-96) rot=(0.57735,0.57735,0.57735;2.0944rad)
FEATURE [Part::Compound] Compound829
  Links = -> [Compound828]
  Placement = pos=(52.33,-52.33,52) rot=(0,0,1;3.92699rad)
FEATURE [Part::Cut] Cut476
  Base = -> Compound817
  Tool = -> Compound829
FEATURE [Part::Cylinder] Cylinder1678  label="Válec1678"
  Angle = 360
  AttacherType = Attacher::AttachEngine3D
  Height = 3
  Placement = pos=(-18,95,-57) rot=(0,0,1;0rad)
  Radius = 3
FEATURE [Part::Cylinder] Cylinder1679  label="Válec1679"
  Angle = 360
  AttacherType = Attacher::AttachEngine3D
  Height = 3
  Placement = pos=(18,95,-57) rot=(0,0,1;0rad)
  Radius = 3
FEATURE [Part::Cylinder] Cylinder1677  label="Válec1677"
  Angle = 360
  AttacherType = Attacher::AttachEngine3D
  Height = 3
  Placement = pos=(-18,85,-57) rot=(0,0,1;0rad)
  Radius = 3
FEATURE [Part::Cylinder] Cylinder1680  label="Válec1680"
  Angle = 360
  AttacherType = Attacher::AttachEngine3D
  Height = 3
  Placement = pos=(18,85,-57) rot=(0,0,1;0rad)
  Radius = 3
FEATURE [Part::Compound] Compound830
  Links = -> [Cylinder1679,Cylinder1680,Cylinder1677,Cylinder1678]
  Placement = pos=(0,0,140) rot=(0,0,1;3.92699rad)
FEATURE [Part::Cylinder] Cylinder1706  label="Válec1706"
  Angle = 360
  AttacherType = Attacher::AttachEngine3D
  Height = 60
  Placement = pos=(18,85,-57) rot=(0,0,1;0rad)
  Radius = 1.5
FEATURE [Part::Cylinder] Cylinder1703  label="Válec1703"
  Angle = 360
  AttacherType = Attacher::AttachEngine3D
  Height = 60
  Placement = pos=(-18,85,-57) rot=(0,0,1;0rad)
  Radius = 1.5
FEATURE [Part::Cylinder] Cylinder1704  label="Válec1704"
  Angle = 360
  AttacherType = Attacher::AttachEngine3D
  Height = 60
  Placement = pos=(-18,95,-57) rot=(0,0,1;0rad)
  Radius = 1.5
FEATURE [Part::Cylinder] Cylinder1705  label="Válec1705"
  Angle = 360
  AttacherType = Attacher::AttachEngine3D
  Height = 60
  Placement = pos=(18,95,-57) rot=(0,0,1;0rad)
  Radius = 1.5
FEATURE [Part::Compound] Compound844
  Links = -> [Cylinder1705,Cylinder1706,Cylinder1703,Cylinder1704]
  Placement = pos=(0,0,100) rot=(0,0,1;3.92699rad)
FEATURE [Part::Cut] Cut487
  Base = -> Cut476
  Tool = -> Compound830
FEATURE [Part::Cut] Cut488
  Base = -> Cut487
  Tool = -> Compound844
FEATURE [Part::Chamfer] Chamfer047
  Base = -> Cut488
  Edges = 2 edges r=3: [Edge11,Edge39]
FEATURE [Part::Chamfer] Chamfer048  label="G-mini_encoder-bottomhold"
  Base = -> Chamfer047
  Edges = 2 edges r=3: [Edge6,Edge23]
  Placement = pos=(0,0,-2) rot=(0,0,1;0rad)
FEATURE [Mesh::Feature] Mesh003  label="G-mini_encoder-sidehold (Meshed)"
FEATURE [Part::FeaturePython] Tube106  # WARN: FeaturePython — macro-defined, semantics opaque (R4)
  AttacherType = Attacher::AttachEngine3D
  Height = 1
  InnerRadius = 4
  OuterRadius = 5
  Placement = pos=(0,90,81) rot=(0,0,1;0rad)
FEATURE [Part::Cylinder] Cylinder2548  label="Válec2518"
  Angle = 360
  AttacherType = Attacher::AttachEngine3D
  Height = 48
  Placement = pos=(0,90,-53) rot=(0,0,1;0rad)
  Radius = 2.6
FEATURE [Part::Cylinder] Cylinder2555  label="Válec2525"
  Angle = 360
  AttacherType = Attacher::AttachEngine3D
  Height = 60
  Placement = pos=(18,85,-57) rot=(0,0,1;0rad)
  Radius = 1.5
FEATURE [Part::Cylinder] Cylinder2552  label="Válec2522"
  Angle = 360
  AttacherType = Attacher::AttachEngine3D
  Height = 60
  Placement = pos=(-18,85,-57) rot=(0,0,1;0rad)
  Radius = 1.5
FEATURE [Part::Box] Box1051  label="Krychle1050"
  AttacherType = Attacher::AttachEngine3D
  Height = 2
  Length = 6
  Placement = pos=(15,92,-56) rot=(0,0,1;0rad)
  Width = 6
FEATURE [Part::Box] Box1046  label="Krychle1045"
  AttacherType = Attacher::AttachEngine3D
  Height = 20
  Length = 22.8
  Placement = pos=(-11.4,-15.34,34) rot=(0,0,1;0rad)
  Width = 34.21
FEATURE [Part::Compound] Compound1134
  Links = -> [Box1046]
  Placement = pos=(0,90,-83) rot=(0,0,1;0rad)
FEATURE [Part::Cylinder] Cylinder2547  label="Válec2517"
  Angle = 360
  AttacherType = Attacher::AttachEngine3D
  Height = 60
  Placement = pos=(-18,95,-57) rot=(0,0,1;0rad)
  Radius = 1.5
FEATURE [Part::Box] Box1047  label="Krychle1046"
  AttacherType = Attacher::AttachEngine3D
  Height = 7
  Length = 42
  Placement = pos=(-21,-12,34) rot=(0,0,1;0rad)
  Width = 24
FEATURE [Part::Compound] Compound1133
  Links = -> [Box1047]
  Placement = pos=(63.64,-63.64,43) rot=(0,0,1;3.92699rad)
FEATURE [Part::Cylinder] Cylinder2550  label="Válec2520"
  Angle = 360
  AttacherType = Attacher::AttachEngine3D
  Height = 5
  Placement = pos=(0,90,77) rot=(0,0,1;0rad)
  Radius = 5
FEATURE [Part::Compound] Compound1137
  Links = -> [Cylinder2550]
  Placement = pos=(0,0,2) rot=(0,0,1;3.92699rad)
FEATURE [Part::Cut] Cut951
  Base = -> Compound1133
  Placement = pos=(0,0,-22) rot=(0,0,1;0rad)
  Tool = -> Compound1137
FEATURE [Part::Cylinder] Cylinder2549  label="Válec2519"
  Angle = 360
  AttacherType = Attacher::AttachEngine3D
  Height = 5
  Placement = pos=(0,90,77) rot=(0,0,1;0rad)
  Radius = 3
FEATURE [Part::Compound] Compound1132
  Links = -> [Cylinder2549]
  Placement = pos=(0,0,-24) rot=(0,0,1;3.92699rad)
FEATURE [Part::Cut] Cut953
  Base = -> Cut951
  Tool = -> Compound1132
FEATURE [Part::Box] Box1050  label="Krychle1049"
  AttacherType = Attacher::AttachEngine3D
  Height = 2
  Length = 6
  Placement = pos=(-21,92,-56) rot=(0,0,1;0rad)
  Width = 6
FEATURE [Part::Box] Box1048  label="Krychle1047"
  AttacherType = Attacher::AttachEngine3D
  Height = 2
  Length = 6
  Placement = pos=(15,82,-56) rot=(0,0,1;0rad)
  Width = 6
FEATURE [Part::Cylinder] Cylinder2551  label="Válec2521"
  Angle = 360
  AttacherType = Attacher::AttachEngine3D
  Height = 60
  Placement = pos=(18,85,-57) rot=(0,0,1;0rad)
  Radius = 1.5
FEATURE [Part::Cylinder] Cylinder2553  label="Válec2523"
  Angle = 360
  AttacherType = Attacher::AttachEngine3D
  Height = 60
  Placement = pos=(-18,95,-57) rot=(0,0,1;0rad)
  Radius = 1.5
FEATURE [Part::Box] Box1049  label="Krychle1048"
  AttacherType = Attacher::AttachEngine3D
  Height = 24
  Length = 36
  Placement = pos=(-18,78,-49) rot=(0,0,1;0rad)
  Width = 24
FEATURE [Part::Cut] Cut950
  Base = -> Box1049
  Placement = pos=(0,0,21) rot=(0,0,1;0rad)
  Tool = -> Compound1134
FEATURE [Part::Cut] Cut949
  Base = -> Cut950
  Tool = -> Cylinder2548
FEATURE [Part::Chamfer] Chamfer108
  Base = -> Cut949
  Edges = 2 edges r=6: [Edge6,Edge8]
FEATURE [Part::Cylinder] Cylinder2554  label="Válec2524"
  Angle = 360
  AttacherType = Attacher::AttachEngine3D
  Height = 60
  Placement = pos=(-18,85,-57) rot=(0,0,1;0rad)
  Radius = 1.5
FEATURE [Part::Cylinder] Cylinder2557  label="Válec2527"
  Angle = 360
  AttacherType = Attacher::AttachEngine3D
  Height = 60
  Placement = pos=(18,95,-57) rot=(0,0,1;0rad)
  Radius = 1.5
FEATURE [Part::Compound] Compound1136
  Links = -> [Cylinder2557,Cylinder2555,Cylinder2554,Cylinder2553]
  Placement = pos=(0,0,100) rot=(0,0,1;3.92699rad)
FEATURE [Part::Box] Box1052  label="Krychle1051"
  AttacherType = Attacher::AttachEngine3D
  Height = 2
  Length = 6
  Placement = pos=(-21,82,-56) rot=(0,0,1;0rad)
  Width = 6
FEATURE [Part::Compound] Compound1135
  Links = -> [Box1052,Box1050,Box1048,Box1051]
  Placement = pos=(0,0,117) rot=(0,0,1;3.92699rad)
FEATURE [Part::Cylinder] Cylinder2556  label="Válec2526"
  Angle = 360
  AttacherType = Attacher::AttachEngine3D
  Height = 60
  Placement = pos=(18,95,-57) rot=(0,0,1;0rad)
  Radius = 1.5
FEATURE [Part::Compound] Compound1131
  Links = -> [Cylinder2556,Cylinder2551,Cylinder2552,Cylinder2547]
  Placement = pos=(0,0,-31) rot=(0,0,1;0rad)
FEATURE [Part::Cut] Cut952
  Base = -> Chamfer108
  Tool = -> Compound1131
FEATURE [Part::Chamfer] Chamfer107
  Base = -> Cut952
  Edges = 2 edges r=3: [Edge25,Edge33]
  Placement = pos=(0,180,0) rot=(0,0,1;3.14159rad)
FEATURE [Part::Compound] Compound1139
  Links = -> [Tube106]
  Placement = pos=(0,0,-24) rot=(0,0,1;3.92699rad)
FEATURE [Part::Compound] Compound1138
  Links = -> [Compound1139,Cut953]
  Placement = pos=(0,0,4) rot=(0,0,1;0rad)
FEATURE [Part::Cut] Cut954
  Base = -> Compound1138
  Tool = -> Compound1136
FEATURE [Part::Cut] Cut955
  Base = -> Cut954
  Tool = -> Compound1135
FEATURE [Part::Chamfer] Chamfer109
  Base = -> Cut955
  Edges = 2 edges r=2: [Edge10,Edge36]
  Placement = pos=(0,180,31) rot=(-0.382683,0.92388,0;3.14159rad)
FEATURE [Part::Compound] Compound1130  label="L-elb_encoder-uphold003"
  Links = -> [Chamfer107,Chamfer109]
  Placement = pos=(0,-174,20) rot=(0,0,1;0rad)
FEATURE [Part::Chamfer] Chamfer110  label="G-mini_encoder-uphold"
  Base = -> Compound1130
  Edges = 2 edges r=2: [Edge18,Edge45]
FEATURE [Mesh::Feature] Mesh004  label="G-mini_encoder-uphold (Meshed)"
FEATURE [Part::Cylinder] Cylinder2367  label="Válec2367"
  Angle = 360
  AttacherType = Attacher::AttachEngine3D
  Height = 4
  Placement = pos=(63.64,-63.64,76) rot=(0,0,1;3.92699rad)
  Radius = 4
FEATURE [Part::Cylinder] Cylinder1692  label="Válec1692"
  Angle = 360
  AttacherType = Attacher::AttachEngine3D
  Height = 60
  Placement = pos=(18,85,-57) rot=(0,0,1;0rad)
  Radius = 1.5
FEATURE [Part::Cylinder] Cylinder1690  label="Válec1690"
  Angle = 360
  AttacherType = Attacher::AttachEngine3D
  Height = 60
  Placement = pos=(-18,95,-57) rot=(0,0,1;0rad)
  Radius = 1.5
FEATURE [Part::Cylinder] Cylinder1691  label="Válec1691"
  Angle = 360
  AttacherType = Attacher::AttachEngine3D
  Height = 60
  Placement = pos=(18,95,-57) rot=(0,0,1;0rad)
  Radius = 1.5
FEATURE [Part::Box] Box930  label="Krychle929"
  AttacherType = Attacher::AttachEngine3D
  Height = 2
  Length = 42
  Placement = pos=(-21,-12,34) rot=(0,0,1;0rad)
  Width = 24
FEATURE [Part::Cylinder] Cylinder1689  label="Válec1689"
  Angle = 360
  AttacherType = Attacher::AttachEngine3D
  Height = 60
  Placement = pos=(-18,85,-57) rot=(0,0,1;0rad)
  Radius = 1.5
FEATURE [Part::Cylinder] Cylinder1760  label="Válec1760"
  Angle = 360
  AttacherType = Attacher::AttachEngine3D
  Height = 4
  Placement = pos=(63.64,-63.64,64) rot=(0,0,1;3.92699rad)
  Radius = 9
FEATURE [Part::Box] Box711  label="Krychle711"
  AttacherType = Attacher::AttachEngine3D
  Height = 4
  Length = 28.8
  Placement = pos=(-14.4,10,24) rot=(0,0,1;0rad)
  Width = 2
FEATURE [Part::Compound] Compound890
  Links = -> [Box711]
  Placement = pos=(63.64,-63.64,38) rot=(0,0,1;3.92699rad)
FEATURE [Part::Compound] Compound818
  Links = -> [Box930]
  Placement = pos=(63.64,-63.64,42) rot=(0,0,1;3.92699rad)
FEATURE [Part::Compound] Compound833
  Links = -> [Cylinder1691,Cylinder1692,Cylinder1689,Cylinder1690]
  Placement = pos=(0,0,100) rot=(0,0,1;3.92699rad)
FEATURE [Part::Cut] Cut472
  Base = -> Compound818
  Placement = pos=(0,0,-10) rot=(0,0,1;0rad)
  Tool = -> Cylinder2367
FEATURE [Part::Cut] Cut481  label="Base_encoder-washer1"
  Base = -> Cut472
  Placement = pos=(0,0,-3) rot=(0,0,1;0rad)
  Tool = -> Compound833
FEATURE [Part::Cut] Cut522
  Base = -> Cut481
  Tool = -> Compound890
FEATURE [Part::Cut] Cut523
  Base = -> Cut522
  Tool = -> Cylinder1760
FEATURE [Part::Chamfer] Chamfer058  label="G-mini_encoder-washer"
  Base = -> Cut523
  Edges = 2 edges r=2: [Edge3,Edge31]
  Placement = pos=(0,6,48) rot=(-0.382683,0.92388,0;3.14159rad)
FEATURE [Mesh::Feature] Mesh005  label="G-mini_encoder-washer (Meshed)"
FEATURE [Mesh::Feature] Mesh006  label="Wrist_outer-halo-encoder (Meshed)001"
FEATURE [Part::Cylinder] Cylinder2811  label="Válec2781"
  Angle = 360
  AttacherType = Attacher::AttachEngine3D
  Height = 5
  Placement = pos=(1.1e-14,-27.5,19.5) rot=(0,0,1;3.14159rad)
  Radius = 3
FEATURE [Part::Cylinder] Cylinder2812  label="Válec2782"
  Angle = 360
  AttacherType = Attacher::AttachEngine3D
  Height = 20
  Placement = pos=(-19.4454,19.4454,19) rot=(0,0,1;0.785398rad)
  Radius = 1.5
FEATURE [Part::Cylinder] Cylinder2813  label="Válec2783"
  Angle = 360
  AttacherType = Attacher::AttachEngine3D
  Height = 20
  Placement = pos=(-19.4454,-19.4454,19) rot=(0,0,1;2.35619rad)
  Radius = 1.5
FEATURE [Part::Box] Box1053  label="Krychle1052"
  AttacherType = Attacher::AttachEngine3D
  Height = 6
  Length = 20
  Placement = pos=(-38,-40,5) rot=(0,0,1;0rad)
  Width = 20
FEATURE [Part::Cylinder] Cylinder2814  label="Válec2784"
  Angle = 360
  AttacherType = Attacher::AttachEngine3D
  Height = 3
  Placement = pos=(-19.4454,-19.4454,19) rot=(0,0,1;2.35619rad)
  Radius = 3
FEATURE [Part::Cylinder] Cylinder2815  label="Válec2785"
  Angle = 360
  AttacherType = Attacher::AttachEngine3D
  Height = 16
  Radius = 36
FEATURE [Part::Cylinder] Cylinder2816  label="Válec2786"
  Angle = 360
  AttacherType = Attacher::AttachEngine3D
  Height = 20
  Placement = pos=(0,27.5,19) rot=(0,0,1;0rad)
  Radius = 1.5
FEATURE [Part::Box] Box1054  label="Krychle1053"
  AttacherType = Attacher::AttachEngine3D
  Height = 32
  Length = 15
  Placement = pos=(-38,-68,5) rot=(0,0,1;0rad)
  Width = 13.5
FEATURE [Part::Cylinder] Cylinder2817  label="Válec2787"
  Angle = 360
  AttacherType = Attacher::AttachEngine3D
  Height = 16
  Radius = 36
FEATURE [Part::Cylinder] Cylinder2818  label="Válec2788"
  Angle = 360
  AttacherType = Attacher::AttachEngine3D
  Height = 16
  Placement = pos=(22,-40,0) rot=(0,0,1;0rad)
  Radius = 8
FEATURE [Part::Box] Box1055  label="Krychle1054"
  AttacherType = Attacher::AttachEngine3D
  Height = 32
  Length = 15
  Placement = pos=(23,-68,5) rot=(0,0,1;0rad)
  Width = 13.5
FEATURE [Part::Cylinder] Cylinder2819  label="Válec2789"
  Angle = 360
  AttacherType = Attacher::AttachEngine3D
  Height = 3
  Placement = pos=(-27.5,-4e-15,19) rot=(0,0,1;1.5708rad)
  Radius = 3
FEATURE [Part::Box] Box1056  label="Krychle1055"
  AttacherType = Attacher::AttachEngine3D
  Height = 6
  Length = 20
  Placement = pos=(18,-40,5) rot=(0,0,1;0rad)
  Width = 20
FEATURE [Part::Cylinder] Cylinder2820  label="Válec2790"
  Angle = 360
  AttacherType = Attacher::AttachEngine3D
  Height = 16
  Placement = pos=(-22,-40,0) rot=(0,0,1;0rad)
  Radius = 8
FEATURE [Part::Cylinder] Cylinder2821  label="Válec2791"
  Angle = 360
  AttacherType = Attacher::AttachEngine3D
  Height = 16
  Radius = 36
FEATURE [Part::Box] Box1057  label="Krychle1056"
  AttacherType = Attacher::AttachEngine3D
  Height = 6
  Length = 8
  Placement = pos=(-38,-79,5) rot=(0,0,1;0rad)
  Width = 80
FEATURE [Part::Box] Box1058  label="Krychle1057"
  AttacherType = Attacher::AttachEngine3D
  Height = 6
  Length = 8
  Placement = pos=(30,-79,5) rot=(0,0,1;0rad)
  Width = 80
FEATURE [Part::Cylinder] Cylinder2822  label="Válec2792"
  Angle = 360
  AttacherType = Attacher::AttachEngine3D
  Height = 3
  Placement = pos=(-19.45,19.45,19) rot=(0,0,1;0.785398rad)
  Radius = 3
FEATURE [Part::Cylinder] Cylinder2823  label="Válec2793"
  Angle = 360
  AttacherType = Attacher::AttachEngine3D
  Height = 3
  Placement = pos=(0,27.5,19) rot=(0,0,1;0rad)
  Radius = 3
FEATURE [Part::Cylinder] Cylinder2824  label="Válec2794"
  Angle = 360
  AttacherType = Attacher::AttachEngine3D
  Height = 3
  Placement = pos=(27.5,1.2e-14,19) rot=(0,0,-1;1.5708rad)
  Radius = 3
FEATURE [Part::Chamfer] Chamfer150
  Base = -> Box1058
  Edges = 1 edges r=1: [Edge6]
FEATURE [Part::Compound] Compound1255
  Links = -> [Cylinder2818,Cylinder2820]
FEATURE [Part::Chamfer] Chamfer154
  Base = -> Box1057
  Edges = 1 edges r=1: [Edge2]
FEATURE [Part::Chamfer] Chamfer149
  Base = -> Chamfer154
  Edges = 1 edges r=1: [Edge15]
FEATURE [Part::Chamfer] Chamfer156
  Base = -> Chamfer150
  Edges = 1 edges r=1: [Edge15]
FEATURE [Part::Compound] Compound1260
  Links = -> [Box1055,Box1054]
  Placement = pos=(0,-17.5,0) rot=(0,0,1;0rad)
FEATURE [Part::Compound] Compound1264
  Links = -> [Box1056,Box1053]
FEATURE [Part::Cut] Cut1073
  Base = -> Compound1264
  Tool = -> Compound1255
FEATURE [Part::Chamfer] Chamfer148
  Base = -> Cut1073
  Edges = 1 edges r=1: [Edge8]
FEATURE [Part::Chamfer] Chamfer153
  Base = -> Chamfer148
  Edges = 1 edges r=1: [Edge8]
FEATURE [Part::Chamfer] Chamfer155
  Base = -> Chamfer153
  Edges = 1 edges r=1: [Edge23]
FEATURE [Part::Chamfer] Chamfer152
  Base = -> Chamfer155
  Edges = 1 edges r=1: [Edge16]
FEATURE [Part::Cut] Cut1074
  Base = -> Chamfer156
  Tool = -> Cylinder2815
FEATURE [Part::Cut] Cut1075
  Base = -> Chamfer152
  Tool = -> Cylinder2821
FEATURE [Part::Cut] Cut1076
  Base = -> Chamfer149
  Tool = -> Cylinder2817
FEATURE [Part::Compound] Compound1256
  Links = -> [Cut1074,Cut1076]
FEATURE [Part::Cut] Cut1078
  Base = -> Compound1256
  Tool = -> Compound1260
FEATURE [Part::FeaturePython] Tube143  # WARN: FeaturePython — macro-defined, semantics opaque (R4)
  AttacherType = Attacher::AttachEngine3D
  Height = 24
  InnerRadius = 22
  OuterRadius = 31
  Placement = pos=(0,-17,37) rot=(1,0,0;1.5708rad)
FEATURE [Part::FeaturePython] Tube144  # WARN: FeaturePython — macro-defined, semantics opaque (R4)
  AttacherType = Attacher::AttachEngine3D
  Height = 1
  InnerRadius = 12
  OuterRadius = 14
  Placement = pos=(0,0,9) rot=(0,0,1;0rad)
FEATURE [Part::Box] Box1059  label="Krychle1058"
  AttacherType = Attacher::AttachEngine3D
  Height = 6
  Length = 6
  Placement = pos=(-36,-27,5) rot=(0,0,1;0rad)
  Width = 2
FEATURE [Part::Cylinder] Cylinder2825  label="Válec2795"
  Angle = 360
  AttacherType = Attacher::AttachEngine3D
  Height = 60
  Placement = pos=(33,-10,8) rot=(1,0,0;1.5708rad)
  Radius = 1.5
FEATURE [Part::Cylinder] Cylinder2826  label="Válec2796"
  Angle = 360
  AttacherType = Attacher::AttachEngine3D
  Height = 6
  Radius = 38
FEATURE [Part::Cylinder] Cylinder2827  label="Válec2797"
  Angle = 360
  AttacherType = Attacher::AttachEngine3D
  Height = 20
  Placement = pos=(27.5,1.2e-14,19) rot=(0,0,-1;1.5708rad)
  Radius = 1.5
FEATURE [Part::Box] Box1060  label="Krychle1059"
  AttacherType = Attacher::AttachEngine3D
  Height = 6
  Length = 6
  Placement = pos=(30,-27,5) rot=(0,0,1;0rad)
  Width = 2
FEATURE [Part::Cylinder] Cylinder2828  label="Válec2798"
  Angle = 360
  AttacherType = Attacher::AttachEngine3D
  Height = 20
  Placement = pos=(1.1e-14,-27.5,19) rot=(0,0,1;3.14159rad)
  Radius = 1.5
FEATURE [Part::Cylinder] Cylinder2829  label="Válec2799"
  Angle = 360
  AttacherType = Attacher::AttachEngine3D
  Height = 5
  Placement = pos=(19.45,-19.45,19.5) rot=(0,0,1;3.92699rad)
  Radius = 3
FEATURE [Part::Cylinder] Cylinder2830  label="Válec2800"
  Angle = 360
  AttacherType = Attacher::AttachEngine3D
  Height = 20
  Placement = pos=(-27.5,-4e-15,19) rot=(0,0,1;1.5708rad)
  Radius = 1.5
FEATURE [Part::Cylinder] Cylinder2831  label="Válec2801"
  Angle = 360
  AttacherType = Attacher::AttachEngine3D
  Height = 20
  Placement = pos=(19.4454,19.4454,19) rot=(0,0,-1;0.785398rad)
  Radius = 1.5
FEATURE [Part::Cylinder] Cylinder2832  label="Válec2802"
  Angle = 360
  AttacherType = Attacher::AttachEngine3D
  Height = 5
  Placement = pos=(0,0,1) rot=(0,0,1;0rad)
  Radius = 14
FEATURE [Part::Cylinder] Cylinder2833  label="Válec2803"
  Angle = 360
  AttacherType = Attacher::AttachEngine3D
  Height = 3
  Placement = pos=(19.4454,19.4454,19) rot=(0,0,-1;0.785398rad)
  Radius = 3
FEATURE [Part::Compound] Compound1261
  Links = -> [Cylinder2823,Cylinder2822,Cylinder2819,Cylinder2814,Cylinder2811,Cylinder2829,Cylinder2824,Cylinder2833]
  Placement = pos=(0,0,-19) rot=(0,0,1;0rad)
FEATURE [Part::Cylinder] Cylinder2834  label="Válec2804"
  Angle = 360
  AttacherType = Attacher::AttachEngine3D
  Height = 20
  Placement = pos=(19.4454,-19.4454,19) rot=(0,0,1;3.92699rad)
  Radius = 1.5
FEATURE [Part::Compound] Compound1265
  Links = -> [Cylinder2816,Cylinder2812,Cylinder2830,Cylinder2813,Cylinder2828,Cylinder2834,Cylinder2827,Cylinder2831]
  Placement = pos=(0,0,-23) rot=(0,0,1;0rad)
FEATURE [Part::Box] Box1061  label="Krychle1060"
  AttacherType = Attacher::AttachEngine3D
  Height = 6
  Length = 6
  Placement = pos=(30,-27,5) rot=(0,0,1;0rad)
  Width = 2
FEATURE [Part::Compound] Compound1258
  Links = -> [Box1061,Box1059]
FEATURE [Part::Cylinder] Cylinder2835  label="Válec2805"
  Angle = 360
  AttacherType = Attacher::AttachEngine3D
  Height = 60
  Placement = pos=(-33,-10,8) rot=(1,0,0;1.5708rad)
  Radius = 1.5
FEATURE [Part::Compound] Compound1259
  Links = -> [Cylinder2835,Cylinder2825]
  Placement = pos=(0,-1,0) rot=(0,0,1;0rad)
FEATURE [Part::Box] Box1062  label="Krychle1061"
  AttacherType = Attacher::AttachEngine3D
  Height = 6
  Length = 6
  Placement = pos=(-36,-27,5) rot=(0,0,1;0rad)
  Width = 2
FEATURE [Part::Compound] Compound1266
  Links = -> [Box1060,Box1062]
FEATURE [Part::Cut] Cut1071
  Base = -> Cut1075
  Tool = -> Compound1266
FEATURE [Part::Cylinder] Cylinder2836  label="Válec2806"
  Angle = 360
  AttacherType = Attacher::AttachEngine3D
  Height = 100
  Placement = pos=(-33,-10,8) rot=(1,0,0;1.5708rad)
  Radius = 1.5
FEATURE [Part::Cylinder] Cylinder2837  label="Válec2807"
  Angle = 360
  AttacherType = Attacher::AttachEngine3D
  Height = 3
  Placement = pos=(-26,14,13) rot=(0,1,0;1.5708rad)
  Radius = 3
FEATURE [Part::Box] Box1063  label="Krychle1062"
  AttacherType = Attacher::AttachEngine3D
  Height = 7
  Length = 6
  Placement = pos=(15,-17,10) rot=(0,0,1;0rad)
  Width = 54
FEATURE [Part::Cylinder] Cylinder2838  label="Válec2808"
  Angle = 360
  AttacherType = Attacher::AttachEngine3D
  Height = 64
  Placement = pos=(-26,1,13) rot=(0,1,0;1.5708rad)
  Radius = 1.5
FEATURE [Part::Box] Box1064  label="Krychle1063"
  AttacherType = Attacher::AttachEngine3D
  Height = 7
  Length = 6
  Placement = pos=(-21,-17,10) rot=(0,0,1;0rad)
  Width = 54
FEATURE [Part::Compound] Compound1263
  Links = -> [Box1063,Box1064]
FEATURE [Part::Cylinder] Cylinder2839  label="Válec2809"
  Angle = 360
  AttacherType = Attacher::AttachEngine3D
  Height = 60
  Placement = pos=(-33,-10,8) rot=(1,0,0;1.5708rad)
  Radius = 1.5
FEATURE [Part::Cylinder] Cylinder2840  label="Válec2810"
  Angle = 360
  AttacherType = Attacher::AttachEngine3D
  Height = 100
  Placement = pos=(33,-10,8) rot=(1,0,0;1.5708rad)
  Radius = 1.5
FEATURE [Part::Compound] Compound1262
  Links = -> [Cylinder2836,Cylinder2840]
  Placement = pos=(0,-1,0) rot=(0,0,1;0rad)
FEATURE [Part::Cylinder] Cylinder2841  label="Válec2811"
  Angle = 360
  AttacherType = Attacher::AttachEngine3D
  Height = 20
  Radius = 38
FEATURE [Part::Cylinder] Cylinder2842  label="Válec2812"
  Angle = 360
  AttacherType = Attacher::AttachEngine3D
  Height = 60
  Placement = pos=(33,-10,8) rot=(1,0,0;1.5708rad)
  Radius = 1.5
FEATURE [Part::Compound] Compound1267
  Links = -> [Cylinder2839,Cylinder2842]
  Placement = pos=(0,-4,0) rot=(0,0,1;0rad)
FEATURE [Part::Cylinder] Cylinder2843  label="Válec2813"
  Angle = 360
  AttacherType = Attacher::AttachEngine3D
  Height = 3
  Placement = pos=(-26,-11,13) rot=(0,1,0;1.5708rad)
  Radius = 3
FEATURE [Part::Cylinder] Cylinder2844  label="Válec2814"
  Angle = 360
  AttacherType = Attacher::AttachEngine3D
  Height = 3
  Placement = pos=(-26,-11,13) rot=(0,1,0;1.5708rad)
  Radius = 3
FEATURE [Part::Cylinder] Cylinder2845  label="Válec2815"
  Angle = 360
  AttacherType = Attacher::AttachEngine3D
  Height = 3
  Placement = pos=(-26,1,13) rot=(0,1,0;1.5708rad)
  Radius = 3
FEATURE [Part::Cylinder] Cylinder2846  label="Válec2816"
  Angle = 360
  AttacherType = Attacher::AttachEngine3D
  Height = 64
  Placement = pos=(-26,-11,13) rot=(0,1,0;1.5708rad)
  Radius = 1.5
FEATURE [Part::Cylinder] Cylinder2847  label="Válec2817"
  Angle = 360
  AttacherType = Attacher::AttachEngine3D
  Height = 64
  Placement = pos=(-26,14,13) rot=(0,1,0;1.5708rad)
  Radius = 1.5
FEATURE [Part::Compound] Compound1268
  Links = -> [Cylinder2838,Cylinder2846,Cylinder2847]
  Placement = pos=(0,-2,1) rot=(0,0,1;0rad)
FEATURE [Part::Cylinder] Cylinder2848  label="Válec2818"
  Angle = 360
  AttacherType = Attacher::AttachEngine3D
  Height = 3
  Placement = pos=(-26,1,13) rot=(0,1,0;1.5708rad)
  Radius = 3
FEATURE [Part::Compound] Compound1269
  Links = -> [Cylinder2848,Cylinder2844,Cylinder2837]
  Placement = pos=(44,-2,1) rot=(0,0,1;0rad)
FEATURE [Part::Cylinder] Cylinder2849  label="Válec2819"
  Angle = 360
  AttacherType = Attacher::AttachEngine3D
  Height = 3
  Placement = pos=(-26,14,13) rot=(0,1,0;1.5708rad)
  Radius = 3
FEATURE [Part::Compound] Compound1270
  Links = -> [Cylinder2845,Cylinder2843,Cylinder2849]
  Placement = pos=(5,-2,1) rot=(0,0,1;0rad)
FEATURE [Part::Box] Box1065  label="Krychle1064"
  AttacherType = Attacher::AttachEngine3D
  Height = 18
  Length = 48
  Placement = pos=(-24,18,13.5) rot=(0,0,1;0rad)
  Width = 20
FEATURE [Part::Common] Common013
  Base = -> Compound1263
  Tool = -> Cylinder2841
FEATURE [Part::Chamfer] Chamfer157
  Base = -> Common013
  Edges = 2 edges r=1: [Edge6,Edge13]
FEATURE [Part::Cut] Cut1081
  Base = -> Chamfer157
  Tool = -> Compound1269
FEATURE [Part::Cut] Cut1079
  Base = -> Cut1081
  Tool = -> Compound1270
FEATURE [Part::Cut] Cut1082
  Base = -> Cut1079
  Tool = -> Compound1268
FEATURE [Part::Cut] Cut1083
  Base = -> Cylinder2826
  Tool = -> Compound1261
FEATURE [Part::Cut] Cut1080
  Base = -> Cut1083
  Tool = -> Compound1265
FEATURE [Part::Cut] Cut1077
  Base = -> Cut1080
  Tool = -> Cylinder2832
FEATURE [Part::Chamfer] Chamfer151
  Base = -> Cut1077
  Edges = 1 edges r=1: [Edge3]
  Placement = pos=(1e-15,0,11) rot=(-0.19509,0.980785,0;3.14159rad)
FEATURE [Part::Cut] Cut1072
  Base = -> Chamfer151
  Tool = -> Tube143
FEATURE [Part::Cut] Cut1069
  Base = -> Cut1072
  Tool = -> Compound1259
FEATURE [Part::Cut] Cut1084
  Base = -> Cut1071
  Tool = -> Compound1267
FEATURE [Part::Cut] Cut1085
  Base = -> Cut1082
  Tool = -> Box1065
FEATURE [Part::Cut] Cut1086
  Base = -> Cut1078
  Tool = -> Compound1258
FEATURE [Part::Cut] Cut1070
  Base = -> Cut1086
  Tool = -> Compound1262
FEATURE [Part::Compound] Compound1257  label="Wrist_side-actuator003"
  Links = -> [Cut1070,Cut1069,Cut1084,Cut1085]
FEATURE [Part::Compound] Compound1271  label="Wrist_side-actuator"
  Links = -> [Tube144,Compound1257]
FEATURE [Mesh::Feature] Mesh007  label="Wrist_side-actuator (Meshed)"
FEATURE [Mesh::Feature] Mesh008  label="G-mini_encoder-holder-front (Meshed)"
FEATURE [Mesh::Feature] Mesh009  label="Wrist_outer-halo-encoder (Meshed)002"
FEATURE [Mesh::Feature] Mesh010  label="Wrist_outer-halo-ring (Meshed)"
FEATURE [Mesh::Feature] Mesh011  label="Wrist_outer-halo-ring (Meshed)001"
FEATURE [Mesh::Feature] Mesh012  label="G-mini_moto-holder-A (Meshed)"
FEATURE [Mesh::Feature] Mesh013  label="G-mini_encoder_front-holder (Meshed)"
FEATURE [Mesh::Feature] Mesh014  label="G-mini_encoder-sidehold (Meshed)001"
FEATURE [Mesh::Feature] Mesh015  label="G-mini_encoder-bottomhold (Meshed)"
FEATURE [Mesh::Feature] Mesh016  label="G-mini_encoder-uphold (Meshed)001"
FEATURE [Mesh::Feature] Mesh017  label="G-mini_encoder-washer (Meshed)001"
FEATURE [Mesh::Feature] Mesh018  label="Wrist_side-actuator (Meshed)001"
